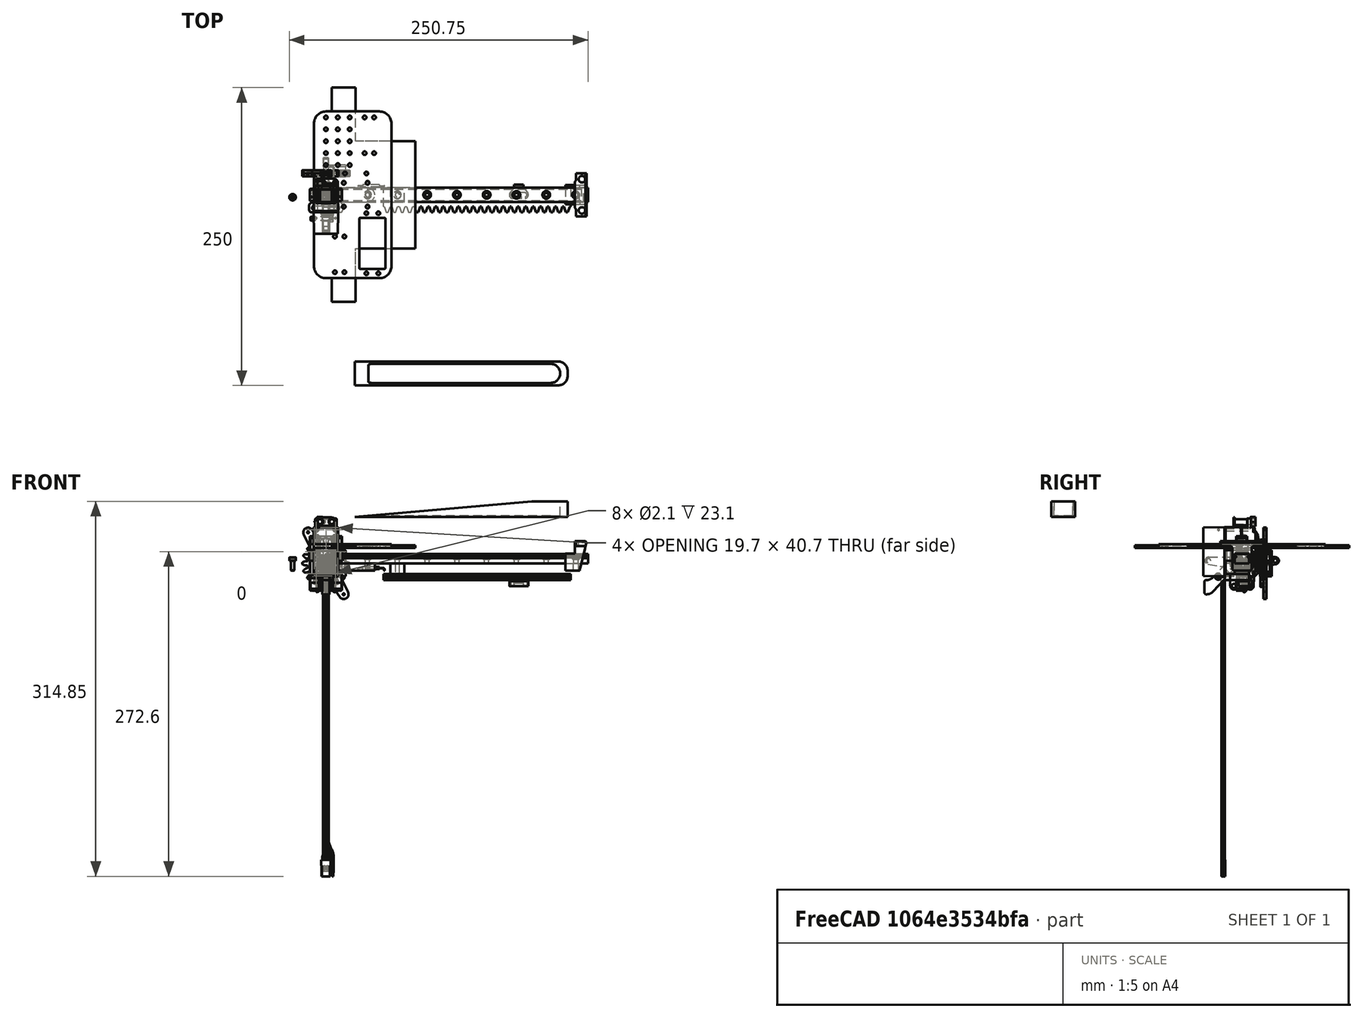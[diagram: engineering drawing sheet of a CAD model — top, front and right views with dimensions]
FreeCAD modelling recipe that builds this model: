
FCSTD DOCUMENT  (FreeCAD 1.0R39285 (Git))
Label: elevateur_canettes
License: All rights reserved
LicenseURL: https://en.wikipedia.org/wiki/All_rights_reserved
objects: Sketcher::SketchObject×58, Part::Feature×46, PartDesign::Pad×32, PartDesign::Pocket×29, PartDesign::Body×22, App::Part×11, Part::FeaturePython×11, PartDesign::Mirrored×11, App::Link×7, PartDesign::LinearPattern×5, PartDesign::Chamfer×4, App::LinkElement×4, PartDesign::PolarPattern×3, PartDesign::FeatureBase×3, PartDesign::MultiTransform×3, PartDesign::Fillet×3, Spreadsheet::Sheet×2, Part::Plane×2, Part::Part2DObjectPython×2, Mesh::Feature×2, +2 more types
note: 456 computed .brp shape members not serialized (recipe doc carries the construction recipe); baked Part::Feature solids carry a one-line shape summary decoded from their .brp
EXTERNAL_REF file=CanaPince.FCStd obj=Part004

FEATURE [Part::Feature] Part__Feature008002002006398  label="MGN12H_EndCap"
  Placement = pos=(5.7441e-12,8.41e-14,21.2) rot=(0,1,0;3.14159rad)
  shape: bbox 26.8 x 9.4 x 5 mm, 23 faces (baked)
FEATURE [Part::Feature] Part__Feature008002002006399  label="MGN12H_EndCap001"
  Placement = pos=(-7.5658e-12,-8.59e-14,-16.2) rot=(0,1,0;3.14159rad)
  shape: bbox 26.8 x 9.4 x 5 mm, 23 faces (baked)
FEATURE [Part::Feature] Part__Feature008002002006400  label="MGN12H_Seal"
  Placement = pos=(-5.6e-15,-0.3,22.7) rot=(0,0,1;0rad)
  shape: bbox 26.8 x 9.4 x 1.7 mm, 155 faces (baked)
FEATURE [Part::Feature] Part__Feature008002002006401  label="MGN12H_Seal001"
  Placement = pos=(-7.2971e-12,-0.3,-22.7) rot=(0,1,0;3.14159rad)
  shape: bbox 26.8 x 9.4 x 1.7 mm, 155 faces (baked)
FEATURE [Part::Feature] Part__Feature008002002006402  label="MGN12H_Cage"
  Placement = pos=(-7.7,-2.54,-20.95) rot=(-0.57735,-0.57735,-0.57735;2.0944rad)
  shape: bbox 3.312 x 0.5 x 42.52 mm, 12 faces (baked)
FEATURE [Part::Feature] Part__Feature008002002006403  label="MGN12H_Cage001"
  Placement = pos=(7.7,-2.79,20.95) rot=(-0.576199,0.576199,0.579647;2.09095rad)
  shape: bbox 3.312 x 0.7505 x 42.52 mm, 12 faces (baked)
FEATURE [Part::Feature] Part__Feature008002002006404  label="MGN12H_Ball"
  Placement = pos=(-6.48,-2.54,19.51) rot=(-0.365574,-0.473745,0.8012;0.619125rad)
  shape: bbox 2.38 x 2.38 x 2.38 mm, 2 faces (baked)
FEATURE [Part::Feature] Part__Feature008002002006405  label="MGN12H_Ball001"
  Placement = pos=(-6.48,-2.54,17.13) rot=(0.592122,0.368399,0.71671;0.865325rad)
  shape: bbox 2.38 x 2.38 x 2.38 mm, 2 faces (baked)
FEATURE [Part::Feature] Part__Feature008002002006406  label="MGN12H_Ball002"
  Placement = pos=(-6.48,-2.54,14.75) rot=(-0.365574,-0.473745,0.8012;0.619125rad)
  shape: bbox 2.38 x 2.38 x 2.38 mm, 2 faces (baked)
FEATURE [Part::Feature] Part__Feature008002002006407  label="MGN12H_Ball003"
  Placement = pos=(-6.48,-2.54,12.37) rot=(-0.365574,-0.473745,0.8012;0.619125rad)
  shape: bbox 2.38 x 2.38 x 2.38 mm, 2 faces (baked)
FEATURE [Part::Feature] Part__Feature008002002006408  label="MGN12H_Ball004"
  Placement = pos=(-6.48,-2.54,9.99) rot=(-0.365574,-0.473745,0.8012;0.619125rad)
  shape: bbox 2.38 x 2.38 x 2.38 mm, 2 faces (baked)
FEATURE [Part::Feature] Part__Feature008002002006409  label="MGN12H_Ball005"
  Placement = pos=(-6.48,-2.54,7.61) rot=(-0.365574,-0.473745,0.8012;0.619125rad)
  shape: bbox 2.38 x 2.38 x 2.38 mm, 2 faces (baked)
FEATURE [Part::Feature] Part__Feature008002002006410  label="MGN12H_Ball006"
  Placement = pos=(-6.48,-2.54,5.23) rot=(-0.365574,-0.473745,0.8012;0.619125rad)
  shape: bbox 2.38 x 2.38 x 2.38 mm, 2 faces (baked)
FEATURE [Part::Feature] Part__Feature008002002006411  label="MGN12H_Ball007"
  Placement = pos=(-6.48,-2.54,2.85) rot=(-0.365574,-0.473745,0.8012;0.619125rad)
  shape: bbox 2.38 x 2.38 x 2.38 mm, 2 faces (baked)
FEATURE [Part::Feature] Part__Feature008002002006412  label="MGN12H_Ball008"
  Placement = pos=(-6.48,-2.54,0.47) rot=(-0.365574,-0.473745,0.8012;0.619125rad)
  shape: bbox 2.38 x 2.38 x 2.38 mm, 2 faces (baked)
FEATURE [Part::Feature] Part__Feature008002002006413  label="MGN12H_Ball009"
  Placement = pos=(-6.48,-2.54,-1.91) rot=(-0.365574,-0.473745,0.8012;0.619125rad)
  shape: bbox 2.38 x 2.38 x 2.38 mm, 2 faces (baked)
FEATURE [Part::Feature] Part__Feature008002002006414  label="MGN12H_Ball010"
  Placement = pos=(-6.48,-2.54,-4.29) rot=(-0.365574,-0.473745,0.8012;0.619125rad)
  shape: bbox 2.38 x 2.38 x 2.38 mm, 2 faces (baked)
FEATURE [Part::Feature] Part__Feature008002002006415  label="MGN12H_Ball011"
  Placement = pos=(-6.48,-2.54,-6.67) rot=(-0.365574,-0.473745,0.8012;0.619125rad)
  shape: bbox 2.38 x 2.38 x 2.38 mm, 2 faces (baked)
FEATURE [Part::Feature] Part__Feature008002002006416  label="MGN12H_Ball012"
  Placement = pos=(-6.48,-2.54,-9.05) rot=(-0.365574,-0.473745,0.8012;0.619125rad)
  shape: bbox 2.38 x 2.38 x 2.38 mm, 2 faces (baked)
FEATURE [Part::Feature] Part__Feature008002002006417  label="MGN12H_Ball013"
  Placement = pos=(-6.48,-2.54,-11.43) rot=(-0.365574,-0.473745,0.8012;0.619125rad)
  shape: bbox 2.38 x 2.38 x 2.38 mm, 2 faces (baked)
FEATURE [Part::Feature] Part__Feature008002002006418  label="MGN12H_Ball014"
  Placement = pos=(-6.48,-2.54,-13.81) rot=(-0.365574,-0.473745,0.8012;0.619125rad)
  shape: bbox 2.38 x 2.38 x 2.38 mm, 2 faces (baked)
FEATURE [Part::Feature] Part__Feature008002002006419  label="MGN12H_Ball015"
  Placement = pos=(-6.48,-2.54,-16.19) rot=(-0.365574,-0.473745,0.8012;0.619125rad)
  shape: bbox 2.38 x 2.38 x 2.38 mm, 2 faces (baked)
FEATURE [Part::Feature] Part__Feature008002002006420  label="MGN12H_Ball016"
  Placement = pos=(-6.48,-2.54,-19.51) rot=(0.61831,0.691205,-0.374071;3.60491rad)
  shape: bbox 2.38 x 2.38 x 2.38 mm, 2 faces (baked)
FEATURE [Part::Feature] Part__Feature008002002006421  label="MGN12H_Ball017"
  Placement = pos=(6.48,-2.54,19.5319) rot=(0.61831,0.691205,-0.374071;3.60491rad)
  shape: bbox 2.38 x 2.38 x 2.38 mm, 2 faces (baked)
FEATURE [Part::Feature] Part__Feature008002002006422  label="MGN12H_Ball018"
  Placement = pos=(6.48,-2.54,17.1519) rot=(0.61831,0.691205,-0.374071;3.60491rad)
  shape: bbox 2.38 x 2.38 x 2.38 mm, 2 faces (baked)
FEATURE [Part::Feature] Part__Feature008002002006423  label="MGN12H_Ball019"
  Placement = pos=(6.48,-2.54,14.7719) rot=(0.61831,0.691205,-0.374071;3.60491rad)
  shape: bbox 2.38 x 2.38 x 2.38 mm, 2 faces (baked)
FEATURE [Part::Feature] Part__Feature008002002006424  label="MGN12H_Ball020"
  Placement = pos=(6.48,-2.54,12.3919) rot=(0.61831,0.691205,-0.374071;3.60491rad)
  shape: bbox 2.38 x 2.38 x 2.38 mm, 2 faces (baked)
FEATURE [Part::Feature] Part__Feature008002002006425  label="MGN12H_Ball021"
  Placement = pos=(6.48,-2.54,10.0119) rot=(0.61831,0.691205,-0.374071;3.60491rad)
  shape: bbox 2.38 x 2.38 x 2.38 mm, 2 faces (baked)
FEATURE [Part::Feature] Part__Feature008002002006426  label="MGN12H_Ball022"
  Placement = pos=(6.48,-2.54,7.63187) rot=(0.61831,0.691205,-0.374071;3.60491rad)
  shape: bbox 2.38 x 2.38 x 2.38 mm, 2 faces (baked)
FEATURE [Part::Feature] Part__Feature008002002006427  label="MGN12H_Ball023"
  Placement = pos=(6.48,-2.54,5.25187) rot=(0.61831,0.691205,-0.374071;3.60491rad)
  shape: bbox 2.38 x 2.38 x 2.38 mm, 2 faces (baked)
FEATURE [Part::Feature] Part__Feature008002002006428  label="MGN12H_Ball024"
  Placement = pos=(6.48,-2.54,2.87187) rot=(0.61831,0.691205,-0.374071;3.60491rad)
  shape: bbox 2.38 x 2.38 x 2.38 mm, 2 faces (baked)
FEATURE [Part::Feature] Part__Feature008002002006429  label="MGN12H_Ball025"
  Placement = pos=(6.48,-2.54,0.491867) rot=(0.61831,0.691205,-0.374071;3.60491rad)
  shape: bbox 2.38 x 2.38 x 2.38 mm, 2 faces (baked)
FEATURE [Part::Feature] Part__Feature008002002006430  label="MGN12H_Ball026"
  Placement = pos=(6.48,-2.54,-1.88813) rot=(0.61831,0.691205,-0.374071;3.60491rad)
  shape: bbox 2.38 x 2.38 x 2.38 mm, 2 faces (baked)
FEATURE [Part::Feature] Part__Feature008002002006431  label="MGN12H_Ball027"
  Placement = pos=(6.48,-2.54,-4.26813) rot=(0.61831,0.691205,-0.374071;3.60491rad)
  shape: bbox 2.38 x 2.38 x 2.38 mm, 2 faces (baked)
FEATURE [Part::Feature] Part__Feature008002002006432  label="MGN12H_Ball028"
  Placement = pos=(6.48,-2.54,-6.64813) rot=(0.61831,0.691205,-0.374071;3.60491rad)
  shape: bbox 2.38 x 2.38 x 2.38 mm, 2 faces (baked)
FEATURE [Part::Feature] Part__Feature008002002006433  label="MGN12H_Ball029"
  Placement = pos=(6.48,-2.54,-9.02813) rot=(0.61831,0.691205,-0.374071;3.60491rad)
  shape: bbox 2.38 x 2.38 x 2.38 mm, 2 faces (baked)
FEATURE [Part::Feature] Part__Feature008002002006434  label="MGN12H_Ball030"
  Placement = pos=(6.48,-2.54,-11.4081) rot=(0.61831,0.691205,-0.374071;3.60491rad)
  shape: bbox 2.38 x 2.38 x 2.38 mm, 2 faces (baked)
FEATURE [Part::Feature] Part__Feature008002002006435  label="MGN12H_Ball031"
  Placement = pos=(6.48,-2.54,-13.7881) rot=(0.61831,0.691205,-0.374071;3.60491rad)
  shape: bbox 2.38 x 2.38 x 2.38 mm, 2 faces (baked)
FEATURE [Part::Feature] Part__Feature008002002006436  label="MGN12H_Ball032"
  Placement = pos=(6.48,-2.54,-16.1681) rot=(0.61831,0.691205,-0.374071;3.60491rad)
  shape: bbox 2.38 x 2.38 x 2.38 mm, 2 faces (baked)
FEATURE [Part::Feature] Part__Feature008002002006437  label="MGN12H_Ball033"
  Placement = pos=(6.48,-2.54,-19.5093) rot=(0.656664,0.517892,-0.548252;3.76753rad)
  shape: bbox 2.38 x 2.38 x 2.38 mm, 2 faces (baked)
FEATURE [Part::Feature] Part__Feature226  label="MGN12H_Body"
  shape: bbox 27 x 10.2 x 48.24 mm, 183 faces (baked)
FEATURE [App::Part] MGN12H001
  Group = -> [Part__Feature226,Part__Feature008002002006398,Part__Feature008002002006399,Part__Feature008002002006400,Part__Feature008002002006401,Part__Feature008002002006402,Part__Feature008002002006403,Part__Feature008002002006404,Part__Feature008002002006405,Part__Feature008002002006406,Part__Feature008002002006407,Part__Feature008002002006408,Part__Feature008002002006409,Part__Feature008002002006410,+27 more]
  Origin = -> Origin263
  Placement = pos=(25,0,8.05) rot=(0.57735,0.57735,0.57735;2.0944rad)
FEATURE [Sketcher::SketchObject] Sketch186
  ArcFitTolerance = 0
  AttachmentSupport = -> [YZ_Plane261]
  FullyConstrained = true
  MakeInternals = false
  MapMode = 5
  Placement = pos=(0,0,0) rot=(0.57735,0.57735,0.57735;2.0944rad)
  sketch-geometry (4):
    g0: LineSegment StartX=-6 StartY=0 StartZ=0 EndX=6 EndY=0 EndZ=0
    g1: LineSegment StartX=6 StartY=0 StartZ=0 EndX=6 EndY=8 EndZ=0
    g2: LineSegment StartX=6 StartY=8 StartZ=0 EndX=-6 EndY=8 EndZ=0
    g3: LineSegment StartX=-6 StartY=8 StartZ=0 EndX=-6 EndY=0 EndZ=0
  constraints (11):
    c: Coincident(g0,g1)
    c: Coincident(g1,g2)
    c: Coincident(g2,g3)
    c: Coincident(g3,g0)
    c: Horizontal(g0)
    c: Horizontal(g2)
    c: Vertical(g1)
    c: Vertical(g3)
    c: Symmetric(g0,g0,g-1)
    c: DistanceX(g0,g0) = 12  'width'
    c: DistanceY(g1,g1) = 8  'height'
FEATURE [PartDesign::Pad] Pad093
  Direction = (1,0,0)
  Length = 220
  Length2 = 10
  Placement = pos=(0,0,0) rot=(0.57735,0.57735,0.57735;2.0944rad)
  Profile = -> Sketch186
  ReferenceAxis = -> Sketch186 [N_Axis]
  Suppressed = false
  Type = 0
  expr: Length = Spreadsheet002.length
FEATURE [Sketcher::SketchObject] Sketch187
  ArcFitTolerance = 0
  AttachmentSupport = -> [YZ_Plane261]
  FullyConstrained = true
  MakeInternals = false
  MapMode = 5
  Placement = pos=(0,0,0) rot=(0.57735,-0.57735,-0.57735;2.0944rad)
  expr: Constraints[13] = <<Sketch186>>.Constraints.width / 2 + 0.3 mm
  sketch-geometry (10):
    g0: ArcOfCircle CenterX=-6.3 CenterY=5.5 CenterZ=0 NormalX=0 NormalY=0 NormalZ=1 AngleXU=0 Radius=1.2 StartAngle=0.429775 EndAngle=5.85341
    g1: LineSegment StartX=-5.20913 StartY=6 StartZ=0 EndX=-4.70913 EndY=6 EndZ=0
    g2: LineSegment StartX=-4.70913 StartY=6 StartZ=0 EndX=-4.70913 EndY=5 EndZ=0
    g3: LineSegment StartX=-4.70913 StartY=5 StartZ=0 EndX=-5.20913 EndY=5 EndZ=0
    g4: LineSegment [constr] StartX=-6.3 StartY=5.5 StartZ=0 EndX=-4.70913 EndY=5.5 EndZ=0
    g5: ArcOfCircle CenterX=6.3 CenterY=5.5 CenterZ=0 NormalX=0 NormalY=0 NormalZ=1 AngleXU=0 Radius=1.2 StartAngle=3.57137 EndAngle=8.995
    g6: LineSegment StartX=5.20913 StartY=6 StartZ=0 EndX=4.70913 EndY=6 EndZ=0
    g7: LineSegment StartX=4.70913 StartY=6 StartZ=0 EndX=4.70913 EndY=5 EndZ=0
    g8: LineSegment StartX=4.70913 StartY=5 StartZ=0 EndX=5.20913 EndY=5 EndZ=0
    g9: LineSegment [constr] StartX=6.3 StartY=5.5 StartZ=0 EndX=4.70913 EndY=5.5 EndZ=0
  constraints (29):
    c: Horizontal(g1)
    c: Coincident(g2,g1)
    c: Vertical(g2)
    c: Coincident(g3,g2)
    c: Horizontal(g3)
    c: Coincident(g4,g0)
    c: Horizontal(g4)
    c: Symmetric(g2,g1,g4)
    c: Coincident(g0,g3)
    c: Coincident(g0,g1)
    c: DistanceY(g2,g2) = 1
    c: DistanceX(g1,g1) = 0.5
    c: DistanceY(g-1,g0) = 5.5
    c: DistanceX(g0,g-1) = 6.3
    c: Horizontal(g6)
    c: Coincident(g7,g6)
    c: Vertical(g7)
    c: Coincident(g8,g7)
    c: Horizontal(g8)
    c: Coincident(g9,g5)
    c: Horizontal(g9)
    c: Symmetric(g7,g6,g9)
    c: Coincident(g5,g8)
    c: Coincident(g5,g6)
    c: Diameter(g5) = 2.4
    c: Symmetric(g4,g9,g-2)
    c: Equal(g2,g7)
    c: Equal(g1,g6)
    c: Equal(g0,g5)
FEATURE [PartDesign::Pocket] Pocket008  label="Balls cut001"
  BaseFeature = -> Pad093
  Direction = (1,0,0)
  Length = 5
  Length2 = 5
  Placement = pos=(0,0,0) rot=(0.57735,0.57735,0.57735;2.0944rad)
  Profile = -> Sketch187
  ReferenceAxis = -> Sketch187 [N_Axis]
  Suppressed = false
  Type = 1
FEATURE [Sketcher::SketchObject] Sketch188
  ArcFitTolerance = 0
  AttachmentOffset = pos=(10,0,0) rot=(0,0,1;1.5708rad)
  AttachmentSupport = -> [XY_Plane261]
  FullyConstrained = true
  MakeInternals = false
  MapMode = 5
  Placement = pos=(10,0,0) rot=(0,0,1;1.5708rad)
  expr: .AttachmentOffset.Base.x = Spreadsheet002.offset
  sketch-geometry (1):
    g0: Circle CenterX=0 CenterY=0 CenterZ=0 NormalX=0 NormalY=0 NormalZ=1 AngleXU=0 Radius=1.75
  constraints (2):
    c: Coincident(g0,g-1)
    c: Diameter(g0) = 3.5
FEATURE [PartDesign::Pocket] Pocket009  label="Screw hole001"
  BaseFeature = -> Pocket008
  Direction = (0,0,-1)
  Length = 5
  Length2 = 5
  Midplane = true
  Placement = pos=(0,0,0) rot=(0.57735,0.57735,0.57735;2.0944rad)
  Profile = -> Sketch188
  ReferenceAxis = -> Sketch188 [N_Axis]
  Suppressed = false
  Type = 1
FEATURE [Sketcher::SketchObject] Sketch189
  ArcFitTolerance = 0
  AttachmentOffset = pos=(10,0,8) rot=(0,0,1;1.5708rad)
  AttachmentSupport = -> [XY_Plane261]
  FullyConstrained = true
  MakeInternals = false
  MapMode = 5
  Placement = pos=(10,0,8) rot=(0,0,1;1.5708rad)
  expr: .AttachmentOffset.Base.x = Spreadsheet002.offset
  expr: .AttachmentOffset.Base.z = Sketch186.Constraints.height
  sketch-geometry (1):
    g0: Circle CenterX=0 CenterY=0 CenterZ=0 NormalX=0 NormalY=0 NormalZ=1 AngleXU=0 Radius=3
  constraints (2):
    c: Coincident(g0,g-1)
    c: Diameter(g0) = 6
FEATURE [PartDesign::Pocket] Pocket072  label="Screw head cut001"
  BaseFeature = -> Pocket009
  Direction = (0,0,-1)
  Length = 4.5
  Length2 = 5
  Placement = pos=(0,0,0) rot=(0.57735,0.57735,0.57735;2.0944rad)
  Profile = -> Sketch189
  ReferenceAxis = -> Sketch189 [N_Axis]
  Suppressed = false
  Type = 0
FEATURE [PartDesign::Chamfer] Chamfer005
  Angle = 45
  Base = -> Pocket072 [Edge47]
  BaseFeature = -> Pocket072
  ChamferType = 0
  FlipDirection = false
  Placement = pos=(0,0,0) rot=(0.57735,0.57735,0.57735;2.0944rad)
  Size = 0.2
  Size2 = 1
  SupportTransform = false
  Suppressed = false
  UseAllEdges = false
FEATURE [PartDesign::LinearPattern] LinearPattern002
  BaseFeature = -> Chamfer005
  Direction = -> Sketch188 [V_Axis]
  Length = 200
  Mode = 0
  Occurrences = 9
  Offset = 25
  Originals = -> [Pocket009,Pocket072,Chamfer005]
  Placement = pos=(0,0,0) rot=(0.57735,0.57735,0.57735;2.0944rad)
  Reversed = true
  Suppressed = false
  TransformMode = 0
  expr: Length = Spreadsheet002.distance
  expr: Occurrences = Spreadsheet002.holes_number
FEATURE [PartDesign::Body] Body071  label="Hiwin rail MGN12R"
  AllowCompound = false
  Group = -> [Sketch186,Pad093,Sketch187,Pocket008,Sketch188,Pocket009,Sketch189,Pocket072,Chamfer005,LinearPattern002]
  Origin = -> Origin264
  Tip = -> LinearPattern002
FEATURE [Sketcher::SketchObject] Sketch190
  ArcFitTolerance = 1e-06
  AttachmentSupport = -> [XZ_Plane265]
  FullyConstrained = true
  MakeInternals = false
  MapMode = 5
  Placement = pos=(0,0,0) rot=(0,0.707107,0.707107;3.14159rad)
  sketch-geometry (9):
    g0: LineSegment StartX=-45 StartY=50 StartZ=0 EndX=-45 EndY=0 EndZ=0
    g1: LineSegment StartX=45 StartY=0 StartZ=0 EndX=45 EndY=50 EndZ=0
    g2: LineSegment StartX=45 StartY=50 StartZ=0 EndX=-45 EndY=50 EndZ=0
    g3: LineSegment StartX=-90 StartY=0 StartZ=0 EndX=-90 EndY=-20 EndZ=0
    g4: LineSegment StartX=-90 StartY=-20 StartZ=0 EndX=90 EndY=-20 EndZ=0
    g5: LineSegment StartX=90 StartY=-20 StartZ=0 EndX=90 EndY=0 EndZ=0
    g6: LineSegment StartX=90 StartY=0 StartZ=0 EndX=45 EndY=0 EndZ=0
    g7: LineSegment StartX=-45 StartY=0 StartZ=0 EndX=-90 EndY=0 EndZ=0
    g8: Circle CenterX=-10 CenterY=10 CenterZ=0 NormalX=0 NormalY=0 NormalZ=1 AngleXU=0 Radius=2
  constraints (25):
    c: Coincident(g1,g2)
    c: Coincident(g2,g0)
    c: Vertical(g0)
    c: Vertical(g1)
    c: PointOnObject(g1,g-1)
    c: Coincident(g3,g4)
    c: Coincident(g4,g5)
    c: Coincident(g5,g6)
    c: Coincident(g7,g3)
    c: Vertical(g3)
    c: Vertical(g5)
    c: Horizontal(g4)
    c: Horizontal(g6)
    c: Coincident(g0,g7)
    c: Coincident(g1,g6)
    c: Horizontal(g7)
    c: Symmetric(g1,g0,g-2)
    c: Symmetric(g3,g5,g-2)
    c: Diameter(g8) = 4
    c: DistanceX(g8,g-1) = 10
    c: Distance(g8,g-1) = 10
    c: DistanceX(g2,g2) = 90
    c: DistanceX(g4,g4) = 180
    c: DistanceY(g0,g0) = 50
    c: DistanceY(g5,g5) = 20
FEATURE [PartDesign::Pad] Pad094
  Direction = (0,1,-2e-16)
  Length = 2
  Length2 = 10
  Placement = pos=(0,0,0) rot=(1,0,0;1.5708rad)
  Profile = -> Sketch190 [Edge4,Edge3,Edge2,Edge1,Edge8,Edge7,Edge6,Edge5]
  ReferenceAxis = -> Sketch190 [N_Axis]
  Suppressed = false
  Type = 0
FEATURE [PartDesign::Pocket] Pocket073
  BaseFeature = -> Pad094
  Direction = (0,-1,2e-16)
  Length = 5
  Length2 = 5
  Placement = pos=(0,0,0) rot=(1,0,0;1.5708rad)
  Profile = -> Sketch190 [Edge9]
  ReferenceAxis = -> Sketch190 [N_Axis]
  Reversed = true
  Suppressed = false
  Type = 0
FEATURE [PartDesign::PolarPattern] PolarPattern010
  Angle = 360
  Axis = -> Sketch190 [N_Axis]
  BaseFeature = -> Pocket073
  Mode = 0
  Occurrences = 4
  Offset = 120
  Originals = -> [Pocket073]
  Placement = pos=(0,0,0) rot=(1,0,0;1.5708rad)
  Suppressed = false
  TransformMode = 0
FEATURE [Sketcher::SketchObject] Sketch191
  ArcFitTolerance = 1e-06
  AttachmentSupport = -> [PolarPattern010]
  FullyConstrained = true
  MakeInternals = false
  MapMode = 5
  Placement = pos=(0,2,0) rot=(-1,0,0;1.5708rad)
FEATURE [PartDesign::Body] Body072  label="plaque_support_leve_gradin"
  AllowCompound = false
  Group = -> [Sketch190,Pad094,Pocket073,PolarPattern010,Sketch191]
  Origin = -> Origin268
  Placement = pos=(25,-2.9e-15,13) rot=(0.57735,0.57735,0.57735;2.0944rad)
  Tip = -> PolarPattern010
FEATURE [Spreadsheet::Sheet] Spreadsheet002  label="Spreadsheet_MGN12"
  cells = A1='Length rail; B1='Длина рельсы, мм; C1(length)=220; D1=325; A2='Holes distance; B2='Расстояние между отверстиями; C2(holes_distance)=25; A3='Holes number; B3='Количество отверстий; C3(holes_number)==floor((length - min_offset * 2) / holes_distance) + 1; A4='Distance end holes; B4='Расстояние между центрами крайних отверстий; C4(distance)==holes_distance * (holes_number - 1); A5='Offset 1st hole; B5='Позиция 1го отверстия; C5(offset)==(length - distance) / 2; A6='Min offset 1st hole; B6='Минимальное расстояние от края до центра 1го отверстия; C6(min_offset)=5
FEATURE [App::Part] Part002003  label="Hiwin MGN013"
  Group = -> [Body071,Spreadsheet002]
  Origin = -> Origin265
FEATURE [Part::Feature] Part__Feature001  label="DA 20_servo001"
  shape: bbox 20.7 x 51.21 x 300.6 mm, 536 faces (baked)
FEATURE [Part::Feature] Part__Feature002  label="1641.21"
  Placement = pos=(-1.33e-14,20.6,2.41e-14) rot=(0,1,0;2.61799rad)
  shape: bbox 24.98 x 5 x 35.96 mm, 19 faces (baked)
FEATURE [Part::Feature] Part__Feature003  label="1641.20"
  Placement = pos=(0,20.6,-1e-16) rot=(0,-1,0;0.523599rad)
  shape: bbox 38 x 5 x 59.96 mm, 25 faces (baked)
FEATURE [Part::Feature] Part__Feature004  label="socket head thin cap screw_din_DIN 7984 - M3 x 6 --- 6N"
  Placement = pos=(8e-16,21.2,-7e-16) rot=(0.694747,-0.694747,0.186157;3.50969rad)
  shape: bbox 5.75 x 8 x 5.75 mm, 21 faces (baked)
FEATURE [Part::Feature] Part__Feature005  label="DA 20_servo002"
  shape: bbox 20.7 x 51.21 x 300.6 mm, 536 faces (baked)
FEATURE [Part::Plane] Plane  label="Plan"
  AttacherType = Attacher::AttachEngine3D
  Length = 100
  Placement = pos=(-50,14.15,-50) rot=(1,0,0;1.5708rad)
  Width = 100
FEATURE [Part::Plane] Plane003  label="Plan003"
  AttacherType = Attacher::AttachEngine3D
  Length = 100
  Placement = pos=(-50,-105,-16.5) rot=(1,0,0;0rad)
  Width = 100
FEATURE [Part::FeaturePython] Slice  # WARN: FeaturePython — macro-defined, semantics opaque (R4)
  Base = -> Part__Feature001
  Mode = 1
  Tolerance = 0
  Tools = -> [Plane]
FEATURE [Part::FeaturePython] Slice_child0  label="Slice.0"  # WARN: FeaturePython — macro-defined, semantics opaque (R4)
  Base = -> Slice
  FilterType = 1
  Invert = false
  OverrideMaxVal = 0
  WindowFrom = 80
  WindowTo = 100
  items = 0
FEATURE [Part::FeaturePython] Slice001  # WARN: FeaturePython — macro-defined, semantics opaque (R4)
  Base = -> Slice_child0
  Mode = 1
  Tolerance = 0
  Tools = -> [Plane003]
FEATURE [Part::FeaturePython] Slice_child1  label="Slice.1"  # WARN: FeaturePython — macro-defined, semantics opaque (R4)
  Base = -> Slice
  FilterType = 1
  Invert = false
  OverrideMaxVal = 0
  WindowFrom = 80
  WindowTo = 100
  items = 1
FEATURE [Part::FeaturePython] Slice001_child1  label="Slice001.1"  # WARN: FeaturePython — macro-defined, semantics opaque (R4)
  Base = -> Slice001
  FilterType = 1
  Invert = false
  OverrideMaxVal = 0
  WindowFrom = 80
  WindowTo = 100
  items = 1
FEATURE [Part::FeaturePython] Slice001_child0  label="Slice001.0"  # WARN: FeaturePython — macro-defined, semantics opaque (R4)
  Base = -> Slice001
  FilterType = 1
  Invert = false
  OverrideMaxVal = 0
  WindowFrom = 80
  WindowTo = 100
  items = 0
FEATURE [PartDesign::FeatureBase] BaseFeature
  BaseFeature = -> Slice_child1
  Suppressed = false
FEATURE [PartDesign::Body] Body  label="pignon"
  AllowCompound = false
  BaseFeature = -> Slice_child1
  Group = -> [BaseFeature]
  Origin = -> Origin001
  Tip = -> BaseFeature
FEATURE [PartDesign::FeatureBase] BaseFeature001
  BaseFeature = -> Slice001_child0
  Suppressed = false
FEATURE [PartDesign::Body] Body001  label="corps"
  AllowCompound = false
  BaseFeature = -> Slice001_child0
  Group = -> [BaseFeature001]
  Origin = -> Origin002
  Tip = -> BaseFeature001
FEATURE [Sketcher::SketchObject] Sketch
  ArcFitTolerance = 1e-06
  AttachmentSupport = -> [XZ_Plane003]
  FullyConstrained = true
  MakeInternals = false
  MapMode = 5
  Placement = pos=(0,0,0) rot=(1,0,0;1.5708rad)
  sketch-geometry (4):
    g0: Circle CenterX=0 CenterY=0 CenterZ=0 NormalX=0 NormalY=0 NormalZ=1 AngleXU=0 Radius=1.5
    g1: Circle CenterX=0 CenterY=0 CenterZ=0 NormalX=0 NormalY=0 NormalZ=1 AngleXU=0 Radius=2.75
    g2: Circle CenterX=0 CenterY=0 CenterZ=0 NormalX=0 NormalY=0 NormalZ=1 AngleXU=0 Radius=4.75
    g3: Circle CenterX=0 CenterY=0 CenterZ=0 NormalX=0 NormalY=0 NormalZ=1 AngleXU=0 Radius=10
  constraints (8):
    c: Diameter(g0) = 3
    c: Coincident(g0,g-1)
    c: Diameter(g1) = 5.5
    c: Coincident(g1,g0)
    c: Diameter(g2) = 9.5
    c: Coincident(g2,g0)
    c: Diameter(g3) = 20
    c: Coincident(g3,g0)
FEATURE [PartDesign::Pad] Pad
  Direction = (0,-1,2e-16)
  Length = 5
  Length2 = 10
  Placement = pos=(0,0,0) rot=(1,0,0;1.5708rad)
  Profile = -> Sketch [Edge3,Edge2]
  ReferenceAxis = -> Sketch [N_Axis]
  Suppressed = false
  Type = 0
FEATURE [PartDesign::Pad] Pad001
  BaseFeature = -> Pad
  Direction = (0,-1,2e-16)
  Length = 2
  Length2 = 10
  Placement = pos=(0,0,0) rot=(1,0,0;1.5708rad)
  Profile = -> Sketch [Edge1,Edge3]
  ReferenceAxis = -> Sketch [N_Axis]
  Suppressed = false
  Type = 0
FEATURE [PartDesign::Pocket] Pocket
  BaseFeature = -> Pad001
  Direction = (0,1,-2e-16)
  Length = 0.6
  Length2 = 5
  Placement = pos=(0,0,0) rot=(1,0,0;1.5708rad)
  Profile = -> Sketch [Edge1,Edge2]
  ReferenceAxis = -> Sketch [N_Axis]
  Reversed = true
  Suppressed = false
  Type = 0
FEATURE [PartDesign::Pad] Pad002
  BaseFeature = -> Pocket
  Direction = (0,-1,2e-16)
  Length = 2
  Length2 = 10
  Placement = pos=(0,0,0) rot=(1,0,0;1.5708rad)
  Profile = -> Sketch [Edge2,Edge4]
  ReferenceAxis = -> Sketch [N_Axis]
  Suppressed = false
  Type = 0
FEATURE [Sketcher::SketchObject] Sketch001
  ArcFitTolerance = 1e-06
  AttachmentSupport = -> [Pad002]
  FullyConstrained = true
  MakeInternals = false
  MapMode = 5
  Placement = pos=(0,0,0) rot=(-1,0,0;1.5708rad)
  sketch-geometry (1):
    g0: Circle CenterX=0 CenterY=7 CenterZ=0 NormalX=0 NormalY=0 NormalZ=1 AngleXU=0 Radius=1
  constraints (3):
    c: Diameter(g0) = 2
    c: PointOnObject(g0,g-2)
    c: DistanceY(g-1,g0) = 7
FEATURE [PartDesign::Pocket] Pocket001
  BaseFeature = -> Pad002
  Direction = (0,-1,-2e-16)
  Length = 5
  Length2 = 5
  Placement = pos=(0,0,0) rot=(1,0,0;1.5708rad)
  Profile = -> Sketch001
  ReferenceAxis = -> Sketch001 [N_Axis]
  Suppressed = false
  Type = 0
FEATURE [PartDesign::PolarPattern] PolarPattern
  Angle = 360
  Axis = -> Sketch001 [N_Axis]
  BaseFeature = -> Pocket001
  Mode = 0
  Occurrences = 12
  Offset = 120
  Originals = -> [Pocket001]
  Placement = pos=(0,0,0) rot=(1,0,0;1.5708rad)
  Suppressed = false
  TransformMode = 0
FEATURE [PartDesign::Body] Body002  label="attachement_base"
  AllowCompound = false
  Group = -> [Sketch,Pad,Pad001,Pocket,Pad002,Sketch001,Pocket001,PolarPattern]
  Origin = -> Origin003
  Placement = pos=(0,20.6,0) rot=(0,0,1;0rad)
  Tip = -> PolarPattern
FEATURE [Sketcher::SketchObject] Sketch002
  ArcFitTolerance = 1e-06
  AttachmentSupport = -> [XZ_Plane004]
  FullyConstrained = true
  MakeInternals = false
  MapMode = 5
  Placement = pos=(0,0,0) rot=(1,0,0;1.5708rad)
  sketch-geometry (4):
    g0: Circle CenterX=0 CenterY=0 CenterZ=0 NormalX=0 NormalY=0 NormalZ=1 AngleXU=0 Radius=1.5
    g1: Circle CenterX=0 CenterY=0 CenterZ=0 NormalX=0 NormalY=0 NormalZ=1 AngleXU=0 Radius=2.75
    g2: Circle CenterX=0 CenterY=0 CenterZ=0 NormalX=0 NormalY=0 NormalZ=1 AngleXU=0 Radius=4.75
    g3: Circle CenterX=0 CenterY=0 CenterZ=0 NormalX=0 NormalY=0 NormalZ=1 AngleXU=0 Radius=20
  constraints (8):
    c: Diameter(g0) = 3
    c: Coincident(g0,g-1)
    c: Diameter(g1) = 5.5
    c: Coincident(g1,g0)
    c: Diameter(g2) = 9.5
    c: Coincident(g2,g0)
    c: Diameter(g3) = 40
    c: Coincident(g3,g0)
FEATURE [PartDesign::Pad] Pad003
  Direction = (0,-1,2e-16)
  Length = 5
  Length2 = 10
  Placement = pos=(0,0,0) rot=(1,0,0;1.5708rad)
  Profile = -> Sketch002 [Edge3,Edge2]
  ReferenceAxis = -> Sketch002 [N_Axis]
  Suppressed = false
  Type = 0
FEATURE [PartDesign::Pad] Pad004
  BaseFeature = -> Pad003
  Direction = (0,-1,2e-16)
  Length = 2
  Length2 = 10
  Placement = pos=(0,0,0) rot=(1,0,0;1.5708rad)
  Profile = -> Sketch002 [Edge1,Edge3]
  ReferenceAxis = -> Sketch002 [N_Axis]
  Suppressed = false
  Type = 0
FEATURE [PartDesign::Pocket] Pocket002
  BaseFeature = -> Pad004
  Direction = (0,1,-2e-16)
  Length = 0.6
  Length2 = 5
  Placement = pos=(0,0,0) rot=(1,0,0;1.5708rad)
  Profile = -> Sketch002 [Edge1,Edge2]
  ReferenceAxis = -> Sketch002 [N_Axis]
  Reversed = true
  Suppressed = false
  Type = 0
FEATURE [PartDesign::Body] Body003  label="pignon001"
  AllowCompound = false
  Group = -> [Sketch002,Pad003,Pad004,Pocket002]
  Origin = -> Origin004
  Placement = pos=(0,20.6,0) rot=(0,1,0;4.71239rad)
  Tip = -> Pocket002
FEATURE [Sketcher::SketchObject] Sketch003
  ArcFitTolerance = 1e-06
  AttachmentSupport = -> [XY_Plane007]
  FullyConstrained = true
  MakeInternals = false
  MapMode = 5
  sketch-geometry (1):
    g0: Circle CenterX=0 CenterY=0 CenterZ=0 NormalX=0 NormalY=0 NormalZ=1 AngleXU=0 Radius=4.75
  constraints (2):
    c: Diameter(g0) = 9.5
    c: Coincident(g0,g-1)
FEATURE [Part::Part2DObjectPython] InvoluteGear  # Draft 2D object (typed FeaturePython)
  AddendumCoefficient = 1
  DedendumCoefficient = 1.25
  ExternalGear = true
  HighPrecision = true
  Modules = 2
  NumberOfTeeth = 18
  PressureAngle = 20
  ProfileShiftCoefficient = 0
  RootFilletCoefficient = 0.38
FEATURE [PartDesign::Pad] Pad005
  Direction = (0,0,1)
  Length = 5
  Length2 = 10
  Profile = -> InvoluteGear
  ReferenceAxis = -> InvoluteGear [N_Axis]
  Reversed = true
  Suppressed = false
  Type = 0
FEATURE [PartDesign::Pocket] Pocket003
  BaseFeature = -> Pad005
  Direction = (0,0,-1)
  Length = 5
  Length2 = 5
  Midplane = true
  Profile = -> Sketch003
  ReferenceAxis = -> Sketch003 [N_Axis]
  Suppressed = false
  Type = 1
FEATURE [PartDesign::Body] Body005  label="pignon002"
  AllowCompound = false
  Group = -> [InvoluteGear,Pad005,Sketch003,Pocket003]
  Origin = -> Origin007
  Placement = pos=(0,20.6,-4.4e-15) rot=(1,0,0;4.71239rad)
  Tip = -> Pocket003
FEATURE [App::Part] Part  label="pignon_servo"
  Group = -> [Body003,Body005]
  Origin = -> Origin006
  Placement = pos=(0,0,0) rot=(0,1,0;4.50295rad)
FEATURE [Part::FeaturePython] InvoluteRack  # WARN: FeaturePython — macro-defined, semantics opaque (R4)
  AttacherType = Attacher::AttachEngine3D
  Placement = pos=(51.5,-12.5,-10.5) rot=(0,0,1;4.71239rad)
  add_endings = true
  clearance = 0.25
  double_helix = false
  head = 0
  head_fillet = 0
  height = 5
  helix_angle = 0
  module = 2
  num_teeth = 25
  pressure_angle = 20
  properties_from_tool = false
  root_fillet = 0
  simplified = false
  thickness = 16
  transverse_pitch = 6.28319
  version = 1.3.0
FEATURE [PartDesign::FeatureBase] BaseFeature002
  BaseFeature = -> InvoluteRack
  Suppressed = false
FEATURE [Sketcher::SketchObject] Sketch192
  ArcFitTolerance = 1e-06
  AttachmentSupport = -> [BaseFeature002]
  FullyConstrained = true
  MakeInternals = false
  MapMode = 5
  Placement = pos=(0,0,5) rot=(0,0,1;0rad)
  sketch-geometry (1):
    g0: Circle CenterX=-12.5 CenterY=8.5 CenterZ=0 NormalX=0 NormalY=0 NormalZ=1 AngleXU=0 Radius=1.7
  constraints (3):
    c: DistanceX(g0) = -12.5
    c: DistanceY(g0) = 8.5
    c: Diameter(g0) = 3.4
FEATURE [PartDesign::Pocket] Pocket074
  BaseFeature = -> BaseFeature002
  Direction = (0,0,-1)
  Length = 5
  Length2 = 5
  Midplane = true
  Profile = -> Sketch192
  ReferenceAxis = -> Sketch192 [N_Axis]
  Suppressed = false
  Type = 1
FEATURE [PartDesign::LinearPattern] LinearPattern
  BaseFeature = -> Pocket074
  Direction = -> Sketch192 [V_Axis]
  Length = 150
  Mode = 0
  Occurrences = 7
  Offset = 25
  Originals = -> [Pocket074]
  Suppressed = false
  TransformMode = 0
FEATURE [Spreadsheet::Sheet] Spreadsheet
  cells = A1='N=Vrot DA20 [tr/min]; B1='omega e [rad/s]; C1='diametre primitif du pignon; D1='vitesse vremaillère [mm/min]; E1='vitesse vremaillère [mm/s]; A2=36; B2==pi * A2 / 30; C2==InvoluteGear.Modules * InvoluteGear.NumberOfTeeth; D2==B2 * C2 / 2; E2==D2 / 60; A3=100; B3==pi * A3 / 30; C3==InvoluteGear.Modules * InvoluteGear.NumberOfTeeth; D3==B3 * C3 / 2; E3==D3 / 60; A7='Distance a parcourir
FEATURE [Sketcher::SketchObject] Sketch193
  ArcFitTolerance = 1e-06
  AttachmentOffset = pos=(0,0,5) rot=(0,0,1;0rad)
  AttachmentSupport = -> [XY_Plane269]
  ExternalGeometry = -> [BaseFeature002]
  FullyConstrained = true
  MakeInternals = false
  MapMode = 5
  Placement = pos=(0,0,5) rot=(0,0,1;0rad)
  sketch-geometry (4):
    g0: LineSegment StartX=-18.5 StartY=-3.14159 StartZ=0 EndX=-6.5 EndY=-3.14159 EndZ=0
    g1: LineSegment StartX=-6.5 StartY=-3.14159 StartZ=0 EndX=-6.5 EndY=153.938 EndZ=0
    g2: LineSegment StartX=-6.5 StartY=153.938 StartZ=0 EndX=-18.5 EndY=153.938 EndZ=0
    g3: LineSegment StartX=-18.5 StartY=153.938 StartZ=0 EndX=-18.5 EndY=-3.14159 EndZ=0
  constraints (10):
    c: Coincident(g0,g1)
    c: Coincident(g1,g2)
    c: Coincident(g2,g3)
    c: Coincident(g3,g0)
    c: Horizontal(g0)
    c: Horizontal(g2)
    c: Vertical(g1)
    c: Distance(g1,g3) = 12
    c: Coincident(g0,g-4)
    c: Coincident(g2,g-3)
FEATURE [Mesh::Feature] open_tin_can
  Placement = pos=(-50,0,0) rot=(-1,0,0;1.5708rad)
FEATURE [Mesh::Feature] open_tin_can001
  Placement = pos=(50,0,0) rot=(-1,0,0;1.5708rad)
FEATURE [App::Part] Part002007  label="canettes"
  Group = -> [open_tin_can,open_tin_can001]
  Origin = -> Origin
  Placement = pos=(0,-100,-17) rot=(0,0,1;0rad)
FEATURE [Sketcher::SketchObject] Sketch194
  ArcFitTolerance = 1e-06
  AttachmentSupport = -> [XZ_Plane270]
  FullyConstrained = true
  MakeInternals = false
  MapMode = 5
  Placement = pos=(0,0,0) rot=(0,0.707107,0.707107;3.14159rad)
  sketch-geometry (17):
    g0: Circle [constr] CenterX=-10 CenterY=10 CenterZ=0 NormalX=0 NormalY=0 NormalZ=1 AngleXU=0 Radius=2
    g1: LineSegment [constr] StartX=-15 StartY=22.5 StartZ=0 EndX=-15 EndY=-22.5 EndZ=0
    g2: LineSegment [constr] StartX=-15 StartY=-22.5 StartZ=0 EndX=15 EndY=-22.5 EndZ=0
    g3: LineSegment [constr] StartX=15 StartY=-22.5 StartZ=0 EndX=15 EndY=22.5 EndZ=0
    g4: LineSegment [constr] StartX=15 StartY=22.5 StartZ=0 EndX=-15 EndY=22.5 EndZ=0
    g5: LineSegment StartX=-60 StartY=30 StartZ=0 EndX=60 EndY=30 EndZ=0
    g6: LineSegment StartX=70 StartY=20 StartZ=0 EndX=70 EndY=-25 EndZ=0
    g7: LineSegment StartX=60 StartY=-35 StartZ=0 EndX=-60 EndY=-35 EndZ=0
    g8: LineSegment StartX=-70 StartY=20 StartZ=0 EndX=-70 EndY=-25 EndZ=0
    g9: ArcOfCircle CenterX=-60 CenterY=20 CenterZ=0 NormalX=0 NormalY=0 NormalZ=1 AngleXU=0 Radius=10 StartAngle=1.5708 EndAngle=3.14159
    g10: GeomPoint [constr] X=-70 Y=30 Z=0
    g11: ArcOfCircle CenterX=-60 CenterY=-25 CenterZ=0 NormalX=0 NormalY=0 NormalZ=1 AngleXU=0 Radius=10 StartAngle=3.14159 EndAngle=4.71239
    g12: GeomPoint [constr] X=-70 Y=-35 Z=0
    g13: ArcOfCircle CenterX=60 CenterY=20 CenterZ=0 NormalX=0 NormalY=0 NormalZ=1 AngleXU=0 Radius=10 StartAngle=0 EndAngle=1.5708
    g14: GeomPoint [constr] X=70 Y=30 Z=0
    g15: ArcOfCircle CenterX=60 CenterY=-25 CenterZ=0 NormalX=0 NormalY=0 NormalZ=1 AngleXU=0 Radius=10 StartAngle=4.71239 EndAngle=6.28319
    g16: GeomPoint [constr] X=70 Y=-35 Z=0
  constraints (41):
    c: Diameter(g0) = 4
    c: DistanceX(g0,g-1) = 10
    c: Distance(g0,g-1) = 10
    c: Coincident(g4,g1)
    c: Vertical(g1)
    c: Vertical(g3)
    c: Horizontal(g2)
    c: Horizontal(g4)
    c: Coincident(g3,g4)
    c: Coincident(g1,g2)
    c: Symmetric(g1,g3,g-1)
    c: DistanceX(g4,g4) = 30
    c: DistanceY(g1,g1) = 45
    c: Vertical(g6)
    c: Horizontal(g7)
    c: Vertical(g8)
    c: Coincident(g2,g3)
    c: Symmetric(g14,g10,g-2)
    c: DistanceY(g16,g-1) = 35
    c: DistanceY(g-1,g14) = 30
    c: DistanceX(g10,g14) = 140
    c: PointOnObject(g10,g5)
    c: PointOnObject(g10,g8)
    c: Tangent(g5,g9) = 1.5708
    c: Tangent(g8,g9) = -1.5708
    c: PointOnObject(g12,g8)
    c: PointOnObject(g12,g7)
    c: Tangent(g8,g11) = -1.5708
    c: Tangent(g7,g11) = 1.5708
    c: PointOnObject(g14,g6)
    c: PointOnObject(g14,g5)
    c: Tangent(g6,g13) = 1.5708
    c: Tangent(g5,g13) = 1.5708
    c: PointOnObject(g16,g6)
    c: PointOnObject(g16,g7)
    c: Tangent(g6,g15) = 1.5708
    c: Tangent(g7,g15) = 1.5708
    c: Equal(g15,g11)
    c: Equal(g11,g9)
    c: Equal(g9,g13)
    c: Radius(g9) = 10
FEATURE [PartDesign::Pad] Pad096
  Direction = (0,1,-2e-16)
  Length = 3
  Length2 = 10
  Placement = pos=(0,0,0) rot=(1,0,0;1.5708rad)
  Profile = -> Sketch194
  ReferenceAxis = -> Sketch194 [N_Axis]
  Suppressed = false
  Type = 0
FEATURE [Sketcher::SketchObject] Sketch195
  ArcFitTolerance = 1e-06
  AttachmentSupport = -> [Pad096]
  FullyConstrained = true
  MakeInternals = false
  MapMode = 5
  Placement = pos=(0,3,0) rot=(-1,0,0;1.5708rad)
  sketch-geometry (1):
    g0: Circle CenterX=10 CenterY=-10 CenterZ=0 NormalX=0 NormalY=0 NormalZ=1 AngleXU=0 Radius=1.5
  constraints (3):
    c: Diameter(g0) = 3
    c: DistanceX(g-1,g0) = 10
    c: DistanceY(g0,g-1) = 10
FEATURE [PartDesign::Pocket] Pocket075  label="fixation_rail"
  BaseFeature = -> Pad096
  Direction = (0,-1,-2e-16)
  Length = 5
  Length2 = 5
  Placement = pos=(0,0,0) rot=(1,0,0;1.5708rad)
  Profile = -> Sketch195
  ReferenceAxis = -> Sketch195 [N_Axis]
  Suppressed = false
  Type = 0
FEATURE [PartDesign::PolarPattern] PolarPattern011
  Angle = 360
  Axis = -> Sketch195 [N_Axis]
  BaseFeature = -> Pocket075
  Mode = 0
  Occurrences = 4
  Offset = 120
  Originals = -> [Pocket075]
  Placement = pos=(0,0,0) rot=(1,0,0;1.5708rad)
  Suppressed = false
  TransformMode = 0
FEATURE [Sketcher::SketchObject] Sketch196
  ArcFitTolerance = 1e-06
  AttachmentOffset = pos=(65,5,0) rot=(0,0,1;0rad)
  AttachmentSupport = -> [PolarPattern011]
  FullyConstrained = true
  MakeInternals = false
  MapMode = 5
  Placement = pos=(65,3,-5) rot=(-1,0,0;1.5708rad)
  sketch-geometry (1):
    g0: Circle CenterX=0 CenterY=0 CenterZ=0 NormalX=0 NormalY=0 NormalZ=1 AngleXU=0 Radius=1.5
  constraints (2):
    c: Diameter(g0) = 3
    c: Coincident(g0,g-1)
FEATURE [PartDesign::Pocket] Pocket076
  BaseFeature = -> PolarPattern011
  Direction = (0,-1,-2e-16)
  Length = 5
  Length2 = 5
  Placement = pos=(0,0,0) rot=(1,0,0;1.5708rad)
  Profile = -> Sketch196
  ReferenceAxis = -> Sketch196 [N_Axis]
  Suppressed = false
  Type = 0
FEATURE [PartDesign::LinearPattern] LinearPattern003
  Direction = -> Sketch196 [H_Axis]
  Length = 40
  Mode = 1
  Occurrences = 5
  Offset = 10
  Placement = pos=(0,0,0) rot=(1,0,0;1.5708rad)
  Reversed = true
  Suppressed = false
  TransformMode = 0
FEATURE [PartDesign::LinearPattern] LinearPattern004
  Direction = -> Sketch196 [V_Axis]
  Length = 20
  Mode = 1
  Occurrences = 3
  Offset = 10
  Placement = pos=(0,0,0) rot=(1,0,0;1.5708rad)
  Suppressed = false
  TransformMode = 0
FEATURE [PartDesign::MultiTransform] MultiTransform
  BaseFeature = -> Pocket076
  Originals = -> [Pocket076]
  Placement = pos=(0,0,0) rot=(1,0,0;1.5708rad)
  Suppressed = false
  TransformMode = 0
  Transformations = -> [LinearPattern003,LinearPattern004]
FEATURE [Sketcher::SketchObject] Sketch197
  ArcFitTolerance = 1e-06
  AttachmentSupport = -> [MultiTransform]
  FullyConstrained = true
  MakeInternals = false
  MapMode = 5
  Placement = pos=(0,3,0) rot=(-1,0,0;1.5708rad)
  sketch-geometry (16):
    g0: Circle CenterX=-66 CenterY=-9 CenterZ=0 NormalX=0 NormalY=0 NormalZ=1 AngleXU=0 Radius=1.5
    g1: Circle CenterX=-66 CenterY=-19 CenterZ=0 NormalX=0 NormalY=0 NormalZ=1 AngleXU=0 Radius=1.5
    g2: Circle CenterX=-15.5 CenterY=-9 CenterZ=0 NormalX=0 NormalY=0 NormalZ=1 AngleXU=0 Radius=1.5
    g3: Circle CenterX=-15.5 CenterY=-19 CenterZ=0 NormalX=0 NormalY=0 NormalZ=1 AngleXU=0 Radius=1.5
    g4: LineSegment [constr] StartX=-61.25 StartY=-4 StartZ=0 EndX=-61.25 EndY=-24 EndZ=0
    g5: LineSegment [constr] StartX=-61.25 StartY=-24 StartZ=0 EndX=-20.25 EndY=-24 EndZ=0
    g6: LineSegment [constr] StartX=-20.25 StartY=-24 StartZ=0 EndX=-20.25 EndY=-4 EndZ=0
    g7: LineSegment [constr] StartX=-20.25 StartY=-4 StartZ=0 EndX=-61.25 EndY=-4 EndZ=0
    g8: LineSegment StartX=-19.25 StartY=-24 StartZ=0 EndX=-19.25 EndY=-4 EndZ=0
    g9: ArcOfCircle CenterX=-20.25 CenterY=-4 CenterZ=0 NormalX=0 NormalY=0 NormalZ=-1 AngleXU=0 Radius=1 StartAngle=1.5708 EndAngle=3.14159
    g10: LineSegment StartX=-20.25 StartY=-3 StartZ=0 EndX=-61.25 EndY=-3 EndZ=0
    g11: ArcOfCircle CenterX=-61.25 CenterY=-4 CenterZ=0 NormalX=0 NormalY=0 NormalZ=-1 AngleXU=0 Radius=1 StartAngle=-1.8e-15 EndAngle=1.5708
    g12: LineSegment StartX=-62.25 StartY=-4 StartZ=0 EndX=-62.25 EndY=-24 EndZ=0
    g13: ArcOfCircle CenterX=-61.25 CenterY=-24 CenterZ=0 NormalX=0 NormalY=0 NormalZ=-1 AngleXU=0 Radius=1 StartAngle=4.71239 EndAngle=6.28319
    g14: LineSegment StartX=-61.25 StartY=-25 StartZ=0 EndX=-20.25 EndY=-25 EndZ=0
    g15: ArcOfCircle CenterX=-20.25 CenterY=-24 CenterZ=0 NormalX=0 NormalY=0 NormalZ=-1 AngleXU=0 Radius=1 StartAngle=3.14159 EndAngle=4.71239
  constraints (40):
    c: Vertical(g2,g3)
    c: Vertical(g0,g1)
    c: Horizontal(g0,g2)
    c: Horizontal(g1,g3)
    c: Equal(g0,g1)
    c: Equal(g1,g2)
    c: Equal(g2,g3)
    c: Diameter(g2) = 3
    c: DistanceY(g3,g2) = 10
    c: DistanceX(g1,g3) = 50.5
    c: DistanceY(g3,g-1) = 19
    c: DistanceX(g3,g-1) = 15.5
    c: Coincident(g4,g5)
    c: Coincident(g5,g6)
    c: Coincident(g6,g7)
    c: Coincident(g7,g4)
    c: Vertical(g4)
    c: Vertical(g6)
    c: Horizontal(g5)
    c: Horizontal(g7)
    c: DistanceX(g7,g7) = 41
    c: DistanceY(g4,g4) = 20
    c: Tangent(g8,g9) = -1.5708
    c: Tangent(g8,g15) = -1.5708
    c: Tangent(g9,g10) = -1.5708
    c: Tangent(g10,g11) = -1.5708
    c: Tangent(g11,g12) = -1.5708
    c: Tangent(g12,g13) = -1.5708
    c: Tangent(g14,g15) = -1.5708
    c: Coincident(g4,g11)
    c: Coincident(g6,g9)
    c: Coincident(g5,g15)
    c: Coincident(g4,g13)
    c: Horizontal(g10)
    c: Vertical(g12)
    c: Vertical(g8)
    c: Radius(g9) = 1
    c: DistanceY(g6,g-1) = 4
    c: DistanceX(g6,g-1) = 20.25
    c: Tangent(g14,g13) = -1.5708
FEATURE [PartDesign::Pocket] Pocket077  label="fixation_servo"
  BaseFeature = -> MultiTransform
  Direction = (0,-1,-2e-16)
  Length = 5
  Length2 = 5
  Placement = pos=(0,0,0) rot=(1,0,0;1.5708rad)
  Profile = -> Sketch197
  ReferenceAxis = -> Sketch197 [N_Axis]
  Suppressed = false
  Type = 0
FEATURE [Sketcher::SketchObject] Sketch198
  ArcFitTolerance = 1e-06
  AttachmentSupport = -> [XY_Plane271]
  FullyConstrained = true
  MakeInternals = false
  MapMode = 5
  sketch-geometry (6):
    g0: ArcOfCircle CenterX=-5 CenterY=0 CenterZ=0 NormalX=0 NormalY=0 NormalZ=1 AngleXU=0 Radius=3 StartAngle=1.5708 EndAngle=4.71239
    g1: ArcOfCircle CenterX=5 CenterY=0 CenterZ=0 NormalX=0 NormalY=0 NormalZ=1 AngleXU=0 Radius=3 StartAngle=4.71239 EndAngle=7.85398
    g2: LineSegment StartX=-5 StartY=3 StartZ=0 EndX=5 EndY=3 EndZ=0
    g3: LineSegment StartX=-5 StartY=-3 StartZ=0 EndX=5 EndY=-3 EndZ=0
    g4: Circle CenterX=-5 CenterY=0 CenterZ=0 NormalX=0 NormalY=0 NormalZ=1 AngleXU=0 Radius=2
    g5: Circle CenterX=5 CenterY=0 CenterZ=0 NormalX=0 NormalY=0 NormalZ=1 AngleXU=0 Radius=2
  constraints (13):
    c: Tangent(g0,g2) = 1.5708
    c: Tangent(g0,g3) = -1.5708
    c: Tangent(g1,g2) = 1.5708
    c: Tangent(g1,g3) = -1.5708
    c: Equal(g0,g1)
    c: Horizontal(g3)
    c: Symmetric(g0,g1,g-1)
    c: DistanceX(g0,g1) = 10
    c: Radius(g0) = 3
    c: Coincident(g4,g0)
    c: Coincident(g5,g1)
    c: Equal(g5,g4)
    c: Diameter(g4) = 4
FEATURE [PartDesign::Pad] Pad097
  Direction = (0,0,1)
  Length = 10.9
  Length2 = 10
  Profile = -> Sketch198
  ReferenceAxis = -> Sketch198 [N_Axis]
  Suppressed = false
  Type = 0
FEATURE [Sketcher::SketchObject] Sketch199
  ArcFitTolerance = 1e-06
  AttachmentSupport = -> [XY_Plane272]
  FullyConstrained = true
  MakeInternals = false
  MapMode = 5
  sketch-geometry (6):
    g0: ArcOfCircle CenterX=-5 CenterY=0 CenterZ=0 NormalX=0 NormalY=0 NormalZ=1 AngleXU=0 Radius=3.5 StartAngle=1.5708 EndAngle=4.71239
    g1: ArcOfCircle CenterX=5 CenterY=0 CenterZ=0 NormalX=0 NormalY=0 NormalZ=1 AngleXU=0 Radius=3.5 StartAngle=4.71239 EndAngle=7.85398
    g2: LineSegment StartX=-5 StartY=3.5 StartZ=0 EndX=5 EndY=3.5 EndZ=0
    g3: LineSegment StartX=-5 StartY=-3.5 StartZ=0 EndX=5 EndY=-3.5 EndZ=0
    g4: Circle CenterX=-5 CenterY=0 CenterZ=0 NormalX=0 NormalY=0 NormalZ=1 AngleXU=0 Radius=2.8
    g5: Circle CenterX=5 CenterY=0 CenterZ=0 NormalX=0 NormalY=0 NormalZ=1 AngleXU=0 Radius=2.8
  constraints (13):
    c: Tangent(g0,g2) = 1.5708
    c: Tangent(g0,g3) = -1.5708
    c: Tangent(g1,g2) = 1.5708
    c: Tangent(g1,g3) = -1.5708
    c: Equal(g0,g1)
    c: Horizontal(g3)
    c: Symmetric(g0,g1,g-1)
    c: DistanceX(g0,g1) = 10
    c: Radius(g0) = 3.5
    c: Coincident(g4,g0)
    c: Coincident(g5,g1)
    c: Equal(g5,g4)
    c: Diameter(g4) = 5.6
FEATURE [PartDesign::Pad] Pad098
  Direction = (0,0,1)
  Length = 1
  Length2 = 10
  Profile = -> Sketch199
  ReferenceAxis = -> Sketch199 [N_Axis]
  Suppressed = false
  Type = 0
FEATURE [PartDesign::Body] Body076  label="DA20_insert"
  AllowCompound = false
  Group = -> [Sketch199,Pad098]
  Origin = -> Origin275
  Placement = pos=(0,-6,35) rot=(0,-0.707107,0.707107;3.14159rad)
  Tip = -> Pad098
FEATURE [Part::FeaturePython] Nut  label="M5-Écrou"  # WARN: FeaturePython — macro-defined, semantics opaque (R4)
  Diameter = 10
  Invert = false
  LeftHanded = false
  MatchOuter = false
  OffsetAngle = 0
  Placement = pos=(-5,11.5,35) rot=(1,0,0;1.5708rad)
  Thread = false
  Type = 19
FEATURE [Part::FeaturePython] Screw  label="M3x10-Vis"  # WARN: FeaturePython — macro-defined, semantics opaque (R4)
  Diameter = 3
  Invert = false
  LeftHanded = false
  Length = 3
  LengthCustom = 10
  MatchOuter = false
  OffsetAngle = 0
  Thread = false
  Type = 52
FEATURE [App::VarSet] VarSet
  Position_elevateur_canette = 124
FEATURE [App::LinkElement] Link_i0
  LinkPlacement = pos=(-4.37114e-07,-7.62939e-06,-5) rot=(0,1,0;3.14159rad)
  LinkedObject = -> <external CanaPince.FCStd>#Part004
  Placement = pos=(-4.37114e-07,-7.62939e-06,-5) rot=(0,1,0;3.14159rad)
  _LinkOwner = 547
FEATURE [App::LinkElement] Link_i1
  LinkPlacement = pos=(100,-8.39233e-05,25.0001) rot=(0,1.00347,0;0rad)
  LinkedObject = -> <external CanaPince.FCStd>#Part004
  Placement = pos=(100,-8.39233e-05,25.0001) rot=(0,1.00347,0;0rad)
  _LinkOwner = 547
FEATURE [App::Link] Link  label="CanaPince_Servomoteur"
  ElementCount = 2
  ElementList = -> [Link_i0,Link_i1]
  LinkPlacement = pos=(14,-50,100) rot=(0.57735,0.57735,0.57735;2.0944rad)
  LinkedObject = -> <external CanaPince.FCStd>#Part004
  Placement = pos=(14,-50,100) rot=(0.57735,0.57735,0.57735;2.0944rad)
FEATURE [Sketcher::SketchObject] Sketch206
  ArcFitTolerance = 1e-06
  AttachmentOffset = pos=(50,11.5,0) rot=(0,0,1;0rad)
  AttachmentSupport = -> [XZ_Plane270]
  FullyConstrained = true
  MakeInternals = false
  MapMode = 5
  Placement = pos=(50,2.6e-15,11.5) rot=(1,0,0;1.5708rad)
  sketch-geometry (1):
    g0: Circle CenterX=15 CenterY=4 CenterZ=0 NormalX=0 NormalY=0 NormalZ=1 AngleXU=0 Radius=1.5
  constraints (3):
    c: Diameter(g0) = 3
    c: DistanceX(g-1,g0) = 15
    c: DistanceY(g-1,g0) = 4
FEATURE [PartDesign::Pocket] Pocket081  label="support_pince_d"
  BaseFeature = -> Pocket077
  Direction = (0,1,-2e-16)
  Length = 5
  Length2 = 5
  Placement = pos=(0,0,0) rot=(1,0,0;1.5708rad)
  Profile = -> Sketch206
  ReferenceAxis = -> Sketch206 [N_Axis]
  Suppressed = false
  Type = 1
FEATURE [PartDesign::Mirrored] Mirrored001
  MirrorPlane = -> Sketch206 [V_Axis]
  Placement = pos=(0,0,0) rot=(1,0,0;1.5708rad)
  Suppressed = false
  TransformMode = 0
FEATURE [PartDesign::Mirrored] Mirrored002
  MirrorPlane = -> Sketch206 [H_Axis]
  Placement = pos=(0,0,0) rot=(1,0,0;1.5708rad)
  Suppressed = false
  TransformMode = 0
FEATURE [PartDesign::MultiTransform] MultiTransform001
  BaseFeature = -> Pocket081
  Originals = -> [Pocket081]
  Placement = pos=(0,0,0) rot=(1,0,0;1.5708rad)
  Suppressed = false
  TransformMode = 0
  Transformations = -> [Mirrored001,Mirrored002]
FEATURE [Sketcher::SketchObject] Sketch207
  ArcFitTolerance = 1e-06
  AttachmentOffset = pos=(-50,-13.5,0) rot=(0,0,1;0rad)
  AttachmentSupport = -> [XZ_Plane270]
  FullyConstrained = true
  MakeInternals = false
  MapMode = 5
  Placement = pos=(-50,-3e-15,-13.5) rot=(1,0,0;1.5708rad)
  sketch-geometry (1):
    g0: Circle CenterX=15 CenterY=4 CenterZ=0 NormalX=0 NormalY=0 NormalZ=1 AngleXU=0 Radius=1.5
  constraints (3):
    c: Diameter(g0) = 3
    c: DistanceX(g-1,g0) = 15
    c: DistanceY(g-1,g0) = 4
FEATURE [PartDesign::Pocket] Pocket082
  BaseFeature = -> MultiTransform001
  Direction = (0,1,-2e-16)
  Length = 5
  Length2 = 5
  Placement = pos=(0,0,0) rot=(1,0,0;1.5708rad)
  Profile = -> Sketch207
  ReferenceAxis = -> Sketch207 [N_Axis]
  Suppressed = false
  Type = 0
FEATURE [PartDesign::Mirrored] Mirrored003
  MirrorPlane = -> Sketch207 [V_Axis]
  Placement = pos=(0,0,0) rot=(1,0,0;1.5708rad)
  Suppressed = false
  TransformMode = 0
FEATURE [PartDesign::Mirrored] Mirrored004
  MirrorPlane = -> Sketch207 [H_Axis]
  Placement = pos=(0,0,0) rot=(1,0,0;1.5708rad)
  Suppressed = false
  TransformMode = 0
FEATURE [PartDesign::MultiTransform] MultiTransform002
  BaseFeature = -> Pocket082
  Originals = -> [Pocket082]
  Placement = pos=(0,0,0) rot=(1,0,0;1.5708rad)
  Suppressed = false
  TransformMode = 0
  Transformations = -> [Mirrored003,Mirrored004]
FEATURE [Sketcher::SketchObject] Sketch208
  ArcFitTolerance = 1e-06
  AttachmentSupport = -> [YZ_Plane274]
  FullyConstrained = true
  MakeInternals = false
  MapMode = 5
  Placement = pos=(0,0,0) rot=(0.57735,0.57735,0.57735;2.0944rad)
  sketch-geometry (14):
    g0: LineSegment StartX=-6.075 StartY=4.075 StartZ=0 EndX=-6.075 EndY=-4.075 EndZ=0
    g1: LineSegment StartX=-6.075 StartY=-4.075 StartZ=0 EndX=6.075 EndY=-4.075 EndZ=0
    g2: LineSegment StartX=6.075 StartY=-4.075 StartZ=0 EndX=6.075 EndY=4.075 EndZ=0
    g3: LineSegment StartX=6.075 StartY=4.075 StartZ=0 EndX=-6.075 EndY=4.075 EndZ=0
    g4: LineSegment StartX=-10.075 StartY=4.075 StartZ=0 EndX=-10.075 EndY=-5.075 EndZ=0
    g5: LineSegment StartX=-7.075 StartY=-8.075 StartZ=0 EndX=7.075 EndY=-8.075 EndZ=0
    g6: LineSegment StartX=10.075 StartY=-5.075 StartZ=0 EndX=10.075 EndY=4.075 EndZ=0
    g7: LineSegment StartX=7.075 StartY=7.075 StartZ=0 EndX=-7.075 EndY=7.075 EndZ=0
    g8: ArcOfCircle CenterX=-7.075 CenterY=4.075 CenterZ=0 NormalX=0 NormalY=0 NormalZ=1 AngleXU=0 Radius=3 StartAngle=1.5708 EndAngle=3.14159
    g9: ArcOfCircle CenterX=-7.075 CenterY=-5.075 CenterZ=0 NormalX=0 NormalY=0 NormalZ=1 AngleXU=0 Radius=3 StartAngle=3.14159 EndAngle=4.71239
    g10: ArcOfCircle CenterX=7.075 CenterY=-5.075 CenterZ=0 NormalX=0 NormalY=0 NormalZ=1 AngleXU=0 Radius=3 StartAngle=4.71239 EndAngle=6.28319
    g11: ArcOfCircle CenterX=7.075 CenterY=4.075 CenterZ=0 NormalX=0 NormalY=0 NormalZ=1 AngleXU=0 Radius=3 StartAngle=0 EndAngle=1.5708
    g12: GeomPoint [constr] X=-10.075 Y=7.075 Z=0
    g13: GeomPoint [constr] X=10.075 Y=-8.075 Z=0
  constraints (34):
    c: Coincident(g0,g1)
    c: Coincident(g1,g2)
    c: Coincident(g2,g3)
    c: Coincident(g3,g0)
    c: Vertical(g0)
    c: Vertical(g2)
    c: Horizontal(g1)
    c: Horizontal(g3)
    c: Symmetric(g2,g0,g-1)
    c: DistanceX(g3,g3) = 12.15
    c: DistanceY(g0,g0) = 8.15
    c: Tangent(g4,g8) = -1.5708
    c: Tangent(g4,g9) = -1.5708
    c: Tangent(g5,g9) = -1.5708
    c: Tangent(g5,g10) = -1.5708
    c: Tangent(g6,g10) = -1.5708
    c: Tangent(g6,g11) = -1.5708
    c: Tangent(g7,g11) = -1.5708
    c: Tangent(g7,g8) = -1.5708
    c: Vertical(g4)
    c: Vertical(g6)
    c: Horizontal(g5)
    c: Horizontal(g7)
    c: Equal(g8,g9)
    c: Equal(g9,g10)
    c: PointOnObject(g12,g4)
    c: PointOnObject(g12,g7)
    c: PointOnObject(g13,g5)
    c: PointOnObject(g13,g6)
    c: Radius(g9) = 3
    c: Symmetric(g11,g8,g-2)
    c: DistanceX(g4,g0) = 4
    c: DistanceY(g0,g7) = 3
    c: DistanceY(g5,g0) = 4
FEATURE [PartDesign::Pad] Pad102
  Direction = (1,0,0)
  Length = 10
  Length2 = 2
  Placement = pos=(0,0,0) rot=(1,1,1;2.0944rad)
  Profile = -> Sketch208
  ReferenceAxis = -> Sketch208 [N_Axis]
  Suppressed = false
  Type = 4
FEATURE [Sketcher::SketchObject] Sketch209
  ArcFitTolerance = 1e-06
  AttachmentSupport = -> [Pad102]
  ExternalGeometry = -> [Pad102]
  FullyConstrained = true
  MakeInternals = false
  MapMode = 5
  Placement = pos=(-2,0,0) rot=(0.57735,0.57735,-0.57735;4.18879rad)
  sketch-geometry (4):
    g0: LineSegment StartX=-6.075 StartY=4.075 StartZ=0 EndX=-6.075 EndY=-4.075 EndZ=0
    g1: LineSegment StartX=-6.075 StartY=-4.075 StartZ=0 EndX=6.075 EndY=-4.075 EndZ=0
    g2: LineSegment StartX=6.075 StartY=-4.075 StartZ=0 EndX=6.075 EndY=4.075 EndZ=0
    g3: LineSegment StartX=6.075 StartY=4.075 StartZ=0 EndX=-6.075 EndY=4.075 EndZ=0
  constraints (10):
    c: Coincident(g0,g1)
    c: Coincident(g1,g2)
    c: Coincident(g2,g3)
    c: Coincident(g3,g0)
    c: Vertical(g0)
    c: Vertical(g2)
    c: Horizontal(g1)
    c: Horizontal(g3)
    c: Coincident(g0,g-3)
    c: Coincident(g1,g-4)
FEATURE [PartDesign::Pad] Pad103
  BaseFeature = -> Pad102
  Direction = (-1,0,0)
  Length = 2
  Length2 = 10
  Placement = pos=(0,0,0) rot=(1,1,1;2.0944rad)
  Profile = -> Sketch209
  ReferenceAxis = -> Sketch209 [N_Axis]
  Refine = true
  Reversed = true
  Suppressed = false
  Type = 0
FEATURE [Sketcher::SketchObject] Sketch210
  ArcFitTolerance = 1e-06
  AttachmentSupport = -> [Pad103]
  ExternalGeometry = -> [Pad103]
  FullyConstrained = true
  MakeInternals = false
  MapMode = 5
  Placement = pos=(-2,0,-1.1e-15) rot=(0.57735,0.57735,-0.57735;4.18879rad)
  sketch-geometry (11):
    g0: ArcOfCircle CenterX=-28 CenterY=1.8 CenterZ=0 NormalX=0 NormalY=0 NormalZ=1 AngleXU=0 Radius=3 StartAngle=1.7489 EndAngle=4.71239
    g1: ArcOfCircle CenterX=-6.8 CenterY=23 CenterZ=0 NormalX=0 NormalY=0 NormalZ=1 AngleXU=0 Radius=3 StartAngle=2e-16 EndAngle=3.1232
    g2: LineSegment StartX=-28.5315 StartY=4.75254 StartZ=0 EndX=-18.1507 EndY=6.62124 EndZ=0
    g3: LineSegment StartX=-28 StartY=-1.2 StartZ=0 EndX=-10.075 EndY=-1.2 EndZ=0
    g4: LineSegment StartX=-9.79949 StartY=23.0552 StartZ=0 EndX=-9.92411 EndY=16.2792 EndZ=0
    g5: LineSegment StartX=-3.8 StartY=23 StartZ=0 EndX=-3.8 EndY=8.075 EndZ=0
    g6: LineSegment StartX=-10.075 StartY=-1.2 StartZ=0 EndX=-3.8 EndY=8.075 EndZ=0
    g7: Circle CenterX=-6.8 CenterY=23 CenterZ=0 NormalX=0 NormalY=0 NormalZ=1 AngleXU=0 Radius=1.75
    g8: Circle CenterX=-28 CenterY=1.8 CenterZ=0 NormalX=0 NormalY=0 NormalZ=1 AngleXU=0 Radius=1.75
    g9: ArcOfCircle CenterX=-19.9224 CenterY=16.463 CenterZ=0 NormalX=0 NormalY=0 NormalZ=1 AngleXU=0 Radius=10 StartAngle=4.8905 EndAngle=6.2648
    g10: GeomPoint [constr] X=-10.075 Y=8.075 Z=0
  constraints (27):
    c: Coincident(g6,g5)
    c: PointOnObject(g5,g-3)
    c: Tangent(g5,g1) = 1.5708
    c: Tangent(g4,g1) = -1.5708
    c: Tangent(g2,g0) = 1.5708
    c: Tangent(g3,g0) = -1.5708
    c: PointOnObject(g3,g-4)
    c: PointOnObject(g10,g-4)
    c: Diameter(g7) = 3.5
    c: Coincident(g7,g1)
    c: Coincident(g8,g0)
    c: Equal(g8,g7)
    c: Equal(g0,g1)
    c: Radius(g1) = 3
    c: DistanceX(g0,g-1) = 28
    c: DistanceY(g-1,g1) = 23
    c: DistanceX(g1,g-1) = 6.8
    c: Coincident(g3,g6)
    c: PointOnObject(g10,g4)
    c: PointOnObject(g10,g2)
    c: Tangent(g4,g9) = 1.5708
    c: Tangent(g2,g9) = -1.5708
    c: Radius(g9) = 10
    c: PointOnObject(g10,g-3)
    c: Horizontal(g3)
    c: Vertical(g5)
    c: DistanceY(g-1,g0) = 1.8
FEATURE [PartDesign::Pad] Pad104
  BaseFeature = -> Pad103
  Direction = (-1,0,0)
  Length = 4
  Length2 = 10
  Placement = pos=(0,0,0) rot=(1,1,1;2.0944rad)
  Profile = -> Sketch210
  ReferenceAxis = -> Sketch210 [N_Axis]
  Refine = true
  Reversed = true
  Suppressed = false
  Type = 0
FEATURE [PartDesign::Fillet] Fillet
  Base = -> Pad104 [Edge11]
  BaseFeature = -> Pad104
  Placement = pos=(0,0,0) rot=(1,1,1;2.0944rad)
  Radius = 3
  SupportTransform = false
  Suppressed = false
  UseAllEdges = false
FEATURE [PartDesign::Mirrored] Mirrored005
  BaseFeature = -> Fillet
  MirrorPlane = -> Sketch210 [V_Axis]
  Originals = -> [Pad104,Fillet]
  Placement = pos=(0,0,0) rot=(1,1,1;2.0944rad)
  Refine = true
  Suppressed = false
  TransformMode = 0
FEATURE [Sketcher::SketchObject] Sketch211
  ArcFitTolerance = 1e-06
  AttachmentSupport = -> [XY_Plane274]
  FullyConstrained = true
  MakeInternals = false
  MapMode = 5
  expr: Constraints[0] = 3.7
  sketch-geometry (1):
    g0: Circle CenterX=10 CenterY=0 CenterZ=0 NormalX=0 NormalY=0 NormalZ=1 AngleXU=0 Radius=1.85
  constraints (3):
    c: Diameter(g0) = 3.7
    c: PointOnObject(g0,g-1)
    c: DistanceX(g-1,g0) = 10
FEATURE [PartDesign::Pocket] Pocket083
  BaseFeature = -> Mirrored005
  Direction = (0,0,-1)
  Length = 5
  Length2 = 5
  Placement = pos=(0,0,0) rot=(1,1,1;2.0944rad)
  Profile = -> Sketch211
  ReferenceAxis = -> Sketch211 [N_Axis]
  Suppressed = false
  Type = 1
FEATURE [Sketcher::SketchObject] Sketch212
  ArcFitTolerance = 1e-06
  AttachmentOffset = pos=(0,0,-4.1) rot=(0,0,1;0rad)
  AttachmentSupport = -> [XY_Plane274]
  ExternalGeometry = -> [Pocket083]
  FullyConstrained = true
  MakeInternals = false
  MapMode = 5
  Placement = pos=(0,0,-4.1) rot=(0,0,1;0rad)
  sketch-geometry (8):
    g0: LineSegment StartX=4.15 StartY=6 StartZ=0 EndX=35 EndY=6 EndZ=0
    g1: ArcOfCircle CenterX=35 CenterY=0 CenterZ=0 NormalX=0 NormalY=0 NormalZ=1 AngleXU=0 Radius=6 StartAngle=0 EndAngle=1.5708
    g2: ArcOfCircle CenterX=10 CenterY=-4.9e-15 CenterZ=0 NormalX=0 NormalY=0 NormalZ=1 AngleXU=0 Radius=1.85 StartAngle=2.7e-15 EndAngle=3.14159
    g3: LineSegment StartX=41 StartY=0 StartZ=0 EndX=36.85 EndY=0 EndZ=0
    g4: LineSegment StartX=33.15 StartY=2e-16 StartZ=0 EndX=11.85 EndY=1e-16 EndZ=0
    g5: LineSegment StartX=4.15 StartY=6 StartZ=0 EndX=4.15 EndY=0 EndZ=0
    g6: ArcOfCircle CenterX=35 CenterY=0 CenterZ=0 NormalX=0 NormalY=0 NormalZ=1 AngleXU=0 Radius=1.85 StartAngle=0 EndAngle=3.14159
    g7: LineSegment StartX=4.15 StartY=3e-16 StartZ=0 EndX=8.15 EndY=3e-16 EndZ=0
  constraints (24):
    c: Horizontal(g0)
    c: PointOnObject(g1,g-1)
    c: PointOnObject(g1,g-1)
    c: Tangent(g1,g0) = 1.5708
    c: DistanceX(g-1,g1) = 35
    c: DistanceY(g-1,g0) = 6
    c: Coincident(g2,g-4)
    c: PointOnObject(g2,g-1)
    c: Coincident(g3,g1)
    c: PointOnObject(g3,g-1)
    c: PointOnObject(g4,g-1)
    c: Coincident(g5,g0)
    c: Coincident(g6,g1)
    c: Coincident(g6,g3)
    c: Coincident(g4,g6)
    c: Equal(g6,g2)
    c: Coincident(g2,g4)
    c: Coincident(g7,g5)
    c: Coincident(g7,g2)
    c: Vertical(g5)
    c: Horizontal(g7)
    c: PointOnObject(g2,g-1)
    c: PointOnObject(g2,g-4)
    c: DistanceX(g7,g7) = 4
FEATURE [PartDesign::Pad] Pad105
  BaseFeature = -> Pocket083
  Direction = (0,0,1)
  Length = 6
  Length2 = 10
  Placement = pos=(0,0,0) rot=(1,1,1;2.0944rad)
  Profile = -> Sketch212
  ReferenceAxis = -> Sketch212 [N_Axis]
  Reversed = true
  Suppressed = false
  Type = 0
FEATURE [PartDesign::Chamfer] Chamfer
  Angle = 45
  Base = -> Pad105 [Edge132]
  BaseFeature = -> Pad105
  ChamferType = 0
  FlipDirection = false
  Placement = pos=(0,0,0) rot=(1,1,1;2.0944rad)
  Size = 2
  Size2 = 1
  SupportTransform = false
  Suppressed = false
  UseAllEdges = false
FEATURE [PartDesign::Mirrored] Mirrored006
  BaseFeature = -> Chamfer
  MirrorPlane = -> XZ_Plane274
  Originals = -> [Pad105,Chamfer]
  Placement = pos=(0,0,0) rot=(1,1,1;2.0944rad)
  Refine = true
  Suppressed = false
  TransformMode = 0
FEATURE [Sketcher::SketchObject] Sketch213
  ArcFitTolerance = 1e-06
  AttachmentSupport = -> [XY_Plane274]
  ExternalGeometry = -> [Mirrored006]
  FullyConstrained = true
  MakeInternals = false
  MapMode = 5
  sketch-geometry (1):
    g0: Circle CenterX=10 CenterY=0 CenterZ=0 NormalX=0 NormalY=0 NormalZ=1 AngleXU=0 Radius=3
  constraints (2):
    c: Diameter(g0) = 6
    c: Coincident(g0,g-3)
FEATURE [PartDesign::Pocket] Pocket084
  BaseFeature = -> Mirrored006
  Direction = (0,0,-1)
  Length = 5
  Length2 = 5
  Placement = pos=(0,0,0) rot=(1,1,1;2.0944rad)
  Profile = -> Sketch213
  ReferenceAxis = -> Sketch213 [N_Axis]
  Reversed = true
  Suppressed = false
  Type = 1
FEATURE [Sketcher::SketchObject] Sketch214
  ArcFitTolerance = 1e-06
  AttachmentSupport = -> [XZ_Plane275]
  FullyConstrained = true
  MakeInternals = false
  MapMode = 5
  Placement = pos=(0,0,0) rot=(1,0,0;1.5708rad)
  sketch-geometry (6):
    g0: LineSegment StartX=-10 StartY=0 StartZ=0 EndX=0 EndY=0 EndZ=0
    g1: LineSegment StartX=-10 StartY=0 StartZ=0 EndX=-10 EndY=-4 EndZ=0
    g2: LineSegment StartX=-8 StartY=-6 StartZ=0 EndX=0 EndY=-6 EndZ=0
    g3: ArcOfCircle CenterX=-8 CenterY=-4 CenterZ=0 NormalX=0 NormalY=0 NormalZ=1 AngleXU=0 Radius=2 StartAngle=3.14159 EndAngle=4.71239
    g4: GeomPoint [constr] X=-10 Y=-6 Z=0
    g5: LineSegment StartX=0 StartY=-6 StartZ=0 EndX=0 EndY=0 EndZ=0
  constraints (15):
    c: Coincident(g0,g-1)
    c: Horizontal(g0)
    c: Coincident(g0,g1)
    c: Horizontal(g2)
    c: Vertical(g1)
    c: PointOnObject(g4,g1)
    c: PointOnObject(g4,g2)
    c: Tangent(g1,g3) = -1.5708
    c: Tangent(g2,g3) = -1.5708
    c: Radius(g3) = 2
    c: DistanceY(g1,g1) = 4
    c: Coincident(g5,g0)
    c: Vertical(g5)
    c: Coincident(g2,g5)
    c: DistanceX(g1,g-1) = 10
FEATURE [PartDesign::Pad] Pad106
  Direction = (0,-1,2e-16)
  Length = 6
  Length2 = 10
  Midplane = true
  Placement = pos=(0,0,0) rot=(1,0,0;1.5708rad)
  Profile = -> Sketch214
  ReferenceAxis = -> Sketch214 [N_Axis]
  Suppressed = false
  Type = 0
FEATURE [Sketcher::SketchObject] Sketch216
  ArcFitTolerance = 1e-06
  AttachmentSupport = -> [Pad106]
  FullyConstrained = true
  MakeInternals = false
  MapMode = 5
  Placement = pos=(0,-2.6e-15,-6) rot=(1,0,0;3.14159rad)
  sketch-geometry (1):
    g0: Circle CenterX=-5 CenterY=0 CenterZ=0 NormalX=0 NormalY=0 NormalZ=1 AngleXU=0 Radius=2.1
  constraints (3):
    c: Diameter(g0) = 4.2
    c: DistanceX(g0,g-1) = 5
    c: PointOnObject(g0,g-1)
FEATURE [PartDesign::Pocket] Pocket086
  BaseFeature = -> Pad106
  Direction = (0,0,1)
  Length = 6
  Length2 = 5
  Placement = pos=(0,0,0) rot=(1,0,0;1.5708rad)
  Profile = -> Sketch216
  ReferenceAxis = -> Sketch216 [N_Axis]
  Suppressed = false
  Type = 0
FEATURE [Sketcher::SketchObject] Sketch220
  ArcFitTolerance = 1e-06
  AttachmentOffset = pos=(18,0,0) rot=(0,0,1;0rad)
  AttachmentSupport = -> [XZ_Plane270]
  FullyConstrained = true
  MakeInternals = false
  MapMode = 5
  Placement = pos=(18,0,0) rot=(1,0,0;1.5708rad)
  sketch-geometry (2):
    g0: Circle CenterX=0 CenterY=9 CenterZ=0 NormalX=0 NormalY=0 NormalZ=1 AngleXU=0 Radius=1.5
    g1: Circle CenterX=0 CenterY=-9 CenterZ=0 NormalX=0 NormalY=0 NormalZ=1 AngleXU=0 Radius=1.5
  constraints (5):
    c: PointOnObject(g0,g-2)
    c: Equal(g1,g0)
    c: Symmetric(g0,g1,g-1)
    c: DistanceY(g-1,g0) = 9
    c: Diameter(g0) = 3
FEATURE [PartDesign::Pocket] Pocket089
  BaseFeature = -> MultiTransform002
  Direction = (0,1,-2e-16)
  Length = 5
  Length2 = 5
  Placement = pos=(0,0,0) rot=(1,0,0;1.5708rad)
  Profile = -> Sketch220
  ReferenceAxis = -> Sketch220 [N_Axis]
  Suppressed = false
  Type = 0
FEATURE [PartDesign::Body] Body074  label="Plaque_interface"
  AllowCompound = false
  Group = -> [Sketch194,Pad096,Sketch195,Pocket075,PolarPattern011,Sketch196,Pocket076,MultiTransform,LinearPattern003,LinearPattern004,Sketch197,Pocket077,Sketch206,Pocket081,MultiTransform001,Mirrored001,Mirrored002,Sketch207,Pocket082,MultiTransform002,Mirrored003,Mirrored004,Sketch220,Pocket089]
  Origin = -> Origin273
  Placement = pos=(25,-2.9e-15,13) rot=(0.57735,0.57735,0.57735;2.0944rad)
  Tip = -> Pocket089
FEATURE [Sketcher::SketchObject] Sketch221
  ArcFitTolerance = 1e-06
  AttachmentSupport = -> [YZ_Plane276]
  FullyConstrained = true
  MakeInternals = false
  MapMode = 5
  Placement = pos=(0,0,0) rot=(0.57735,0.57735,0.57735;2.0944rad)
  sketch-geometry (1):
    g0: Circle CenterX=0 CenterY=0 CenterZ=0 NormalX=0 NormalY=0 NormalZ=1 AngleXU=0 Radius=1
  constraints (2):
    c: Diameter(g0) = 2
    c: Coincident(g0,g-1)
FEATURE [PartDesign::Pad] Pad108
  Direction = (1,0,0)
  Length = 7
  Length2 = 10
  Placement = pos=(0,0,0) rot=(1,1,1;2.0944rad)
  Profile = -> Sketch221
  ReferenceAxis = -> Sketch221 [N_Axis]
  Suppressed = false
  Type = 0
FEATURE [Sketcher::SketchObject] Sketch222
  ArcFitTolerance = 1e-06
  AttachmentSupport = -> [Pad108]
  FullyConstrained = true
  MakeInternals = false
  MapMode = 5
  Placement = pos=(7,0,0) rot=(0.57735,0.57735,0.57735;2.0944rad)
  sketch-geometry (1):
    g0: Circle CenterX=0 CenterY=0 CenterZ=0 NormalX=0 NormalY=0 NormalZ=1 AngleXU=0 Radius=0.25
  constraints (2):
    c: Diameter(g0) = 0.5
    c: Coincident(g0,g-1)
FEATURE [Sketcher::SketchObject] Sketch223
  ArcFitTolerance = 1e-06
  AttachmentSupport = -> [XZ_Plane276]
  ExternalGeometry = -> [Pad108]
  FullyConstrained = true
  MakeInternals = false
  MapMode = 5
  Placement = pos=(0,0,0) rot=(1,0,0;1.5708rad)
  sketch-geometry (4):
    g0: LineSegment StartX=7 StartY=0 StartZ=0 EndX=10 EndY=0 EndZ=0
    g1: LineSegment StartX=11 StartY=-1 StartZ=0 EndX=11 EndY=-2 EndZ=0
    g2: ArcOfCircle CenterX=10 CenterY=-1 CenterZ=0 NormalX=0 NormalY=0 NormalZ=1 AngleXU=0 Radius=1 StartAngle=0 EndAngle=1.5708
    g3: GeomPoint [constr] X=11 Y=0 Z=0
  constraints (11):
    c: Horizontal(g0)
    c: Vertical(g1)
    c: PointOnObject(g3,g0)
    c: PointOnObject(g3,g1)
    c: Tangent(g0,g2) = 1.5708
    c: Tangent(g1,g2) = 1.5708
    c: PointOnObject(g0,g-3)
    c: PointOnObject(g0,g-1)
    c: Radius(g2) = 1
    c: DistanceX(g0,g1) = 4
    c: DistanceY(g1,g0) = 2
FEATURE [PartDesign::AdditivePipe] AdditivePipe
  AuxilleryCurvelinear = true
  AuxillerySpineTangent = false
  BaseFeature = -> Pad108
  Binormal = (0,0,0)
  Mode = 0
  Placement = pos=(0,0,0) rot=(1,1,1;2.0944rad)
  Profile = -> Sketch222
  Spine = -> Sketch223
  SpineTangent = false
  Suppressed = false
  Transformation = 0
  Transition = 0
FEATURE [PartDesign::Mirrored] Mirrored008
  BaseFeature = -> AdditivePipe
  MirrorPlane = -> YZ_Plane276
  Placement = pos=(0,0,0) rot=(1,1,1;2.0944rad)
  Refine = true
  Suppressed = false
  TransformMode = 1
FEATURE [PartDesign::Body] Body080  label="capteur_reed"
  AllowCompound = false
  Group = -> [Sketch221,Pad108,Sketch222,Sketch223,AdditivePipe,Mirrored008]
  Origin = -> Origin279
  Placement = pos=(38,7.5,-4) rot=(0,0,1;0rad)
  Tip = -> Mirrored008
FEATURE [App::Link] Link001  label="capteur_reed001"
  LinkPlacement = pos=(124,0,0) rot=(0,0,1;0rad)
  LinkTransform = true
  LinkedObject = -> Body080
  Placement = pos=(124,0,0) rot=(0,0,1;0rad)
FEATURE [Sketcher::SketchObject] Sketch224
  ArcFitTolerance = 1e-06
  AttachmentSupport = -> [Pocket084]
  ExternalGeometry = -> [Pocket084]
  FullyConstrained = true
  MakeInternals = false
  MapMode = 5
  Placement = pos=(-1.2e-15,6.8e-15,-4.1) rot=(0,0,-1;1.5708rad)
  sketch-geometry (2):
    g0: Circle CenterX=0 CenterY=35 CenterZ=0 NormalX=0 NormalY=0 NormalZ=1 AngleXU=0 Radius=2.1
    g1: Circle CenterX=1.06e-14 CenterY=10 CenterZ=0 NormalX=0 NormalY=0 NormalZ=1 AngleXU=0 Radius=2.1
  constraints (4):
    c: Diameter(g0) = 4.2
    c: Coincident(g0,g-3)
    c: Coincident(g1,g-4)
    c: Diameter(g1) = 4.2
FEATURE [PartDesign::Pocket] Pocket090  label="insert"
  BaseFeature = -> Pocket084
  Direction = (0,1.4e-15,-1)
  Length = 3
  Length2 = 5
  Placement = pos=(0,0,0) rot=(1,1,1;2.0944rad)
  Profile = -> Sketch224
  ReferenceAxis = -> Sketch224 [N_Axis]
  Suppressed = false
  Type = 0
FEATURE [Sketcher::SketchObject] Sketch227
  ArcFitTolerance = 1e-06
  AttachmentSupport = -> [YZ_Plane277]
  FullyConstrained = true
  MakeInternals = false
  MapMode = 5
  Placement = pos=(0,0,0) rot=(0.57735,0.57735,0.57735;2.0944rad)
  sketch-geometry (1):
    g0: Circle CenterX=0 CenterY=0 CenterZ=0 NormalX=0 NormalY=0 NormalZ=1 AngleXU=0 Radius=1.05
  constraints (2):
    c: Diameter(g0) = 2.1
    c: Coincident(g0,g-1)
FEATURE [Sketcher::SketchObject] Sketch228
  ArcFitTolerance = 1e-06
  AttachmentSupport = -> [XY_Plane277]
  FullyConstrained = true
  MakeInternals = false
  MapMode = 5
  sketch-geometry (4):
    g0: LineSegment StartX=-4 StartY=1 StartZ=0 EndX=-4 EndY=-1.5 EndZ=0
    g1: LineSegment StartX=-4 StartY=-1.5 StartZ=0 EndX=4 EndY=-1.5 EndZ=0
    g2: LineSegment StartX=4 StartY=-1.5 StartZ=0 EndX=4 EndY=1 EndZ=0
    g3: LineSegment StartX=4 StartY=1 StartZ=0 EndX=-4 EndY=1 EndZ=0
  constraints (11):
    c: Coincident(g0,g1)
    c: Coincident(g1,g2)
    c: Coincident(g2,g3)
    c: Coincident(g3,g0)
    c: Vertical(g0)
    c: Vertical(g2)
    c: Horizontal(g1)
    c: Symmetric(g2,g0,g-2)
    c: DistanceY(g-1,g0) = 1
    c: DistanceX(g3,g3) = 8
    c: DistanceY(g1,g-1) = 1.5
FEATURE [PartDesign::Pad] Pad110
  Direction = (0,0,1)
  Length = 2
  Length2 = 6
  Profile = -> Sketch228
  ReferenceAxis = -> Sketch228 [N_Axis]
  Suppressed = false
  Type = 4
FEATURE [PartDesign::Pocket] Pocket092
  BaseFeature = -> Pad110
  Direction = (-1,0,0)
  Length = 5
  Length2 = 5
  Midplane = true
  Profile = -> Sketch227
  ReferenceAxis = -> Sketch227 [N_Axis]
  Suppressed = false
  Type = 1
FEATURE [Sketcher::SketchObject] Sketch229
  ArcFitTolerance = 1e-06
  AttachmentSupport = -> [Pocket092]
  ExternalGeometry = -> [Pocket092]
  FullyConstrained = true
  MakeInternals = false
  MapMode = 5
  Placement = pos=(0,0,-6) rot=(1,0,0;3.14159rad)
  expr: Constraints[14] = 3.5 / 2
  sketch-geometry (9):
    g0: ArcOfCircle CenterX=-5 CenterY=7.5 CenterZ=0 NormalX=0 NormalY=0 NormalZ=1 AngleXU=0 Radius=1.75 StartAngle=1.5708 EndAngle=4.71239
    g1: LineSegment StartX=-5 StartY=9.25 StartZ=0 EndX=0 EndY=9.25 EndZ=0
    g2: LineSegment StartX=-5 StartY=5.75 StartZ=0 EndX=0 EndY=5.75 EndZ=0
    g3: LineSegment StartX=0 StartY=1.5 StartZ=0 EndX=-4 EndY=1.5 EndZ=0
    g4: LineSegment StartX=0 StartY=10.5 StartZ=0 EndX=-5 EndY=10.5 EndZ=0
    g5: LineSegment StartX=0 StartY=10.5 StartZ=0 EndX=0 EndY=9.25 EndZ=0
    g6: LineSegment StartX=0 StartY=5.75 StartZ=0 EndX=0 EndY=1.5 EndZ=0
    g7: ArcOfCircle CenterX=-5 CenterY=7.5 CenterZ=0 NormalX=0 NormalY=0 NormalZ=1 AngleXU=0 Radius=3 StartAngle=1.5708 EndAngle=3.8225
    g8: LineSegment StartX=-4 StartY=1.5 StartZ=0 EndX=-7.331 EndY=5.6115 EndZ=0
  constraints (23):
    c: Tangent(g0,g1) = 1.5708
    c: Tangent(g0,g2) = -1.5708
    c: Horizontal(g2)
    c: PointOnObject(g1,g-2)
    c: PointOnObject(g2,g-2)
    c: Horizontal(g1)
    c: Symmetric(g-3,g-3,g3)
    c: Coincident(g3,g-3)
    c: PointOnObject(g4,g-2)
    c: Horizontal(g4)
    c: Coincident(g5,g4)
    c: Coincident(g5,g1)
    c: Coincident(g6,g2)
    c: Coincident(g6,g3)
    c: Radius(g0) = 1.75
    c: Vertical(g1,g4)
    c: DistanceX(g0,g2) = 5
    c: DistanceY(g-1,g0) = 7.5
    c: Coincident(g7,g0)
    c: Coincident(g7,g4)
    c: Coincident(g8,g3)
    c: Tangent(g8,g7) = 1.5708
    c: Radius(g7) = 3
FEATURE [PartDesign::Pad] Pad111
  BaseFeature = -> Pocket092
  Direction = (0,0,-1)
  Length = 4
  Length2 = 10
  Profile = -> Sketch229
  ReferenceAxis = -> Sketch229 [N_Axis]
  Reversed = true
  Suppressed = false
  Type = 0
FEATURE [PartDesign::Mirrored] Mirrored009
  BaseFeature = -> Pad111
  MirrorPlane = -> Sketch229 [V_Axis]
  Originals = -> [Pad111]
  Refine = true
  Suppressed = false
  TransformMode = 0
FEATURE [PartDesign::Fillet] Fillet001
  Base = -> Mirrored009 [Edge16,Edge19]
  BaseFeature = -> Mirrored009
  Radius = 0.4
  SupportTransform = false
  Suppressed = false
  UseAllEdges = false
FEATURE [PartDesign::Chamfer] Chamfer006
  Angle = 45
  Base = -> Fillet001 [Edge26]
  BaseFeature = -> Fillet001
  ChamferType = 0
  FlipDirection = false
  Size = 2
  Size2 = 2
  SupportTransform = false
  Suppressed = false
  UseAllEdges = false
FEATURE [PartDesign::Body] Body081  label="support_capteur_reed"
  AllowCompound = false
  Group = -> [Sketch227,Sketch228,Pad110,Pocket092,Sketch229,Pad111,Mirrored009,Fillet001,Chamfer006]
  Origin = -> Origin280
  Placement = pos=(162,7.5,-13) rot=(0,0,1;0rad)
  Tip = -> Chamfer006
FEATURE [Sketcher::SketchObject] Sketch230
  ArcFitTolerance = 1e-06
  AttachmentSupport = -> [LinearPattern]
  ExternalGeometry = -> [LinearPattern]
  FullyConstrained = true
  MakeInternals = false
  MapMode = 5
  Placement = pos=(0,0,0) rot=(1,0,0;3.14159rad)
  sketch-geometry (1):
    g0: Circle CenterX=-12.5 CenterY=-108.5 CenterZ=0 NormalX=0 NormalY=0 NormalZ=1 AngleXU=0 Radius=1.7
  constraints (2):
    c: Coincident(g0,g-3)
    c: Equal(g0,g-3)
FEATURE [PartDesign::Pad] Pad112
  BaseFeature = -> LinearPattern
  Direction = (0,0,-1)
  Length = 5
  Length2 = 10
  Profile = -> Sketch230
  ReferenceAxis = -> Sketch230 [N_Axis]
  Reversed = true
  Suppressed = false
  Type = 0
FEATURE [Sketcher::SketchObject] Sketch233
  ArcFitTolerance = 1e-06
  AttachmentSupport = -> [Pad112]
  FullyConstrained = true
  MakeInternals = false
  MapMode = 5
  Placement = pos=(0,0,0) rot=(1,0,0;3.14159rad)
  sketch-geometry (11):
    g0: LineSegment StartX=-16.5 StartY=-107.5 StartZ=0 EndX=-16.5 EndY=-113.5 EndZ=0
    g1: LineSegment StartX=-14.5 StartY=-115.5 StartZ=0 EndX=-10.5 EndY=-115.5 EndZ=0
    g2: LineSegment StartX=-8.5 StartY=-113.5 StartZ=0 EndX=-8.5 EndY=-107.5 EndZ=0
    g3: LineSegment StartX=-10.5 StartY=-105.5 StartZ=0 EndX=-14.5 EndY=-105.5 EndZ=0
    g4: ArcOfCircle CenterX=-14.5 CenterY=-107.5 CenterZ=0 NormalX=0 NormalY=0 NormalZ=1 AngleXU=0 Radius=2 StartAngle=1.5708 EndAngle=3.14159
    g5: ArcOfCircle CenterX=-14.5 CenterY=-113.5 CenterZ=0 NormalX=0 NormalY=0 NormalZ=1 AngleXU=0 Radius=2 StartAngle=3.14159 EndAngle=4.71239
    g6: ArcOfCircle CenterX=-10.5 CenterY=-113.5 CenterZ=0 NormalX=0 NormalY=0 NormalZ=1 AngleXU=0 Radius=2 StartAngle=4.71239 EndAngle=6.28319
    g7: ArcOfCircle CenterX=-10.5 CenterY=-107.5 CenterZ=0 NormalX=0 NormalY=0 NormalZ=1 AngleXU=0 Radius=2 StartAngle=-1.8e-15 EndAngle=1.5708
    g8: GeomPoint [constr] X=-16.5 Y=-105.5 Z=0
    g9: GeomPoint [constr] X=-8.5 Y=-115.5 Z=0
    g10: GeomPoint X=-12.5 Y=-110.5 Z=0
  constraints (25):
    c: Tangent(g0,g4) = -1.5708
    c: Tangent(g0,g5) = -1.5708
    c: Tangent(g1,g5) = -1.5708
    c: Tangent(g1,g6) = -1.5708
    c: Tangent(g2,g6) = -1.5708
    c: Tangent(g2,g7) = -1.5708
    c: Tangent(g3,g7) = -1.5708
    c: Tangent(g3,g4) = -1.5708
    c: Vertical(g0)
    c: Vertical(g2)
    c: Horizontal(g1)
    c: Horizontal(g3)
    c: Equal(g4,g5)
    c: Equal(g5,g6)
    c: Equal(g6,g7)
    c: PointOnObject(g8,g0)
    c: PointOnObject(g8,g3)
    c: PointOnObject(g9,g1)
    c: PointOnObject(g9,g2)
    c: Symmetric(g7,g5,g10)
    c: DistanceX(g10,g-1) = 12.5
    c: DistanceY(g10,g-1) = 110.5
    c: Radius(g4) = 2
    c: DistanceY(g1,g3) = 10
    c: DistanceX(g0,g2) = 8
FEATURE [PartDesign::Pad] Pad113
  BaseFeature = -> Pad112
  Direction = (0,0,-1)
  Length = 1
  Length2 = 10
  Profile = -> Sketch233
  ReferenceAxis = -> Sketch233 [N_Axis]
  Suppressed = false
  Type = 0
FEATURE [Sketcher::SketchObject] Sketch231
  ArcFitTolerance = 1e-06
  AttachmentSupport = -> [Pad113]
  FullyConstrained = true
  MakeInternals = false
  MapMode = 5
  Placement = pos=(0,0,-1) rot=(1,0,0;3.14159rad)
  sketch-geometry (1):
    g0: Circle CenterX=-12.5 CenterY=-110.5 CenterZ=0 NormalX=0 NormalY=0 NormalZ=1 AngleXU=0 Radius=1.85
  constraints (3):
    c: Diameter(g0) = 3.7
    c: DistanceY(g0,g-1) = 110.5
    c: DistanceX(g0,g-1) = 12.5
FEATURE [Sketcher::SketchObject] Sketch232
  ArcFitTolerance = 1e-06
  AttachmentSupport = -> [Pad113]
  FullyConstrained = true
  MakeInternals = false
  MapMode = 5
  Placement = pos=(0,0,-1) rot=(1,0,0;3.14159rad)
  sketch-geometry (1):
    g0: Circle CenterX=-12.5 CenterY=-110.5 CenterZ=0 NormalX=0 NormalY=0 NormalZ=1 AngleXU=0 Radius=2.1
  constraints (2):
    c: Diameter(g0) = 4.2
    c: Coincident(g0,g-3)
FEATURE [PartDesign::Pocket] Pocket094
  BaseFeature = -> Pad113
  Direction = (0,0,1)
  Length = 3
  Length2 = 5
  Profile = -> Sketch232
  ReferenceAxis = -> Sketch232 [N_Axis]
  Suppressed = false
  Type = 0
FEATURE [PartDesign::Pocket] Pocket093
  BaseFeature = -> Pocket094
  Direction = (0,0,1)
  Length = 6
  Length2 = 5
  Profile = -> Sketch231
  ReferenceAxis = -> Sketch231 [N_Axis]
  Suppressed = false
  Type = 0
FEATURE [PartDesign::Body] Body073  label="crémaillère"
  AllowCompound = false
  BaseFeature = -> InvoluteRack
  Group = -> [BaseFeature002,Sketch192,Pocket074,LinearPattern,Sketch193,Sketch230,Pad112,Sketch231,Sketch233,Pad113,Pocket094,Pocket093,Sketch232]
  Origin = -> Origin272
  Placement = pos=(51.5,-12.5,-14) rot=(0,0,1;4.71239rad)
  Tip = -> LinearPattern
FEATURE [Sketcher::SketchObject] Sketch240
  ArcFitTolerance = 1e-06
  AttachmentSupport = -> [XY_Plane279]
  FullyConstrained = true
  MakeInternals = false
  MapMode = 5
  sketch-geometry (5):
    g0: LineSegment StartX=-6 StartY=6 StartZ=0 EndX=-6 EndY=-6 EndZ=0
    g1: LineSegment StartX=-6 StartY=-6 StartZ=0 EndX=6 EndY=-6 EndZ=0
    g2: LineSegment StartX=6 StartY=-6 StartZ=0 EndX=6 EndY=6 EndZ=0
    g3: LineSegment StartX=6 StartY=6 StartZ=0 EndX=-6 EndY=6 EndZ=0
    g4: Circle CenterX=0 CenterY=0 CenterZ=0 NormalX=0 NormalY=0 NormalZ=1 AngleXU=0 Radius=1.75
  constraints (13):
    c: Coincident(g0,g1)
    c: Coincident(g1,g2)
    c: Coincident(g2,g3)
    c: Coincident(g3,g0)
    c: Vertical(g0)
    c: Vertical(g2)
    c: Horizontal(g1)
    c: Horizontal(g3)
    c: Diameter(g4) = 3.5
    c: Coincident(g4,g-1)
    c: Symmetric(g2,g0,g4)
    c: Equal(g3,g0)
    c: DistanceX(g3,g3) = 12
FEATURE [PartDesign::Pad] Pad116
  Direction = (0,0,1)
  Length = 9
  Length2 = 10
  Profile = -> Sketch240
  ReferenceAxis = -> Sketch240 [N_Axis]
  Suppressed = false
  Type = 0
FEATURE [PartDesign::Body] Body083  label="cremaillere_spacer"
  AllowCompound = false
  Group = -> [Sketch240,Pad116]
  Origin = -> Origin282
  Placement = pos=(60,0,-9) rot=(0,0,1;0rad)
  Tip = -> Pad116
FEATURE [App::Link] Link002  label="cremaillere_spacer001"
  LinkPlacement = pos=(125,0,0) rot=(0,0,1;0rad)
  LinkTransform = true
  LinkedObject = -> Body083
  Placement = pos=(125,0,0) rot=(0,0,1;0rad)
FEATURE [Sketcher::SketchObject] Sketch241
  ArcFitTolerance = 1e-06
  AttachmentSupport = -> [YZ_Plane282]
  FullyConstrained = true
  MakeInternals = false
  MapMode = 5
  Placement = pos=(0,0,0) rot=(0.57735,0.57735,0.57735;2.0944rad)
  expr: Constraints[48] = 135
  sketch-geometry (23):
    g0: LineSegment StartX=-10 StartY=5.25 StartZ=0 EndX=-10 EndY=-4.25 EndZ=0
    g1: LineSegment StartX=-9.5 StartY=-4.75 StartZ=0 EndX=-6.15 EndY=-4.75 EndZ=0
    g2: LineSegment StartX=10 StartY=-4.25 StartZ=0 EndX=10 EndY=4.25 EndZ=0
    g3: LineSegment StartX=9.5 StartY=4.75 StartZ=0 EndX=-1.8e-15 EndY=4.75 EndZ=0
    g4: ArcOfCircle CenterX=-9.5 CenterY=5.25 CenterZ=0 NormalX=0 NormalY=0 NormalZ=1 AngleXU=0 Radius=0.5 StartAngle=1.5708 EndAngle=3.14159
    g5: ArcOfCircle CenterX=-9.5 CenterY=-4.25 CenterZ=0 NormalX=0 NormalY=0 NormalZ=1 AngleXU=0 Radius=0.5 StartAngle=3.14159 EndAngle=4.71239
    g6: ArcOfCircle CenterX=9.5 CenterY=-4.25 CenterZ=0 NormalX=0 NormalY=0 NormalZ=1 AngleXU=0 Radius=0.5 StartAngle=4.71239 EndAngle=6.28319
    g7: ArcOfCircle CenterX=9.5 CenterY=4.25 CenterZ=0 NormalX=0 NormalY=0 NormalZ=1 AngleXU=0 Radius=0.5 StartAngle=0 EndAngle=1.5708
    g8: GeomPoint [constr] X=-10 Y=4.75 Z=0
    g9: GeomPoint [constr] X=10 Y=-4.75 Z=0
    g10: Circle CenterX=-4.65 CenterY=-2.1 CenterZ=0 NormalX=0 NormalY=0 NormalZ=1 AngleXU=0 Radius=1.15
    g11: Circle CenterX=4.65 CenterY=-2.1 CenterZ=0 NormalX=0 NormalY=0 NormalZ=1 AngleXU=0 Radius=1.15
    g12: LineSegment StartX=-1.2e-15 StartY=4.75 StartZ=0 EndX=-1 EndY=5.75 EndZ=0
    g13: LineSegment StartX=-1 StartY=5.75 StartZ=0 EndX=-9.5 EndY=5.75 EndZ=0
    g14: LineSegment StartX=-6.15 StartY=-4.75 StartZ=0 EndX=-5.9 EndY=-4.95 EndZ=0
    g15: LineSegment StartX=-5.9 StartY=-4.95 StartZ=0 EndX=-3.4 EndY=-4.95 EndZ=0
    g16: LineSegment StartX=-3.4 StartY=-4.95 StartZ=0 EndX=-3.15 EndY=-4.75 EndZ=0
    g17: LineSegment StartX=3.15 StartY=-4.75 StartZ=0 EndX=3.4 EndY=-4.95 EndZ=0
    g18: LineSegment StartX=3.4 StartY=-4.95 StartZ=0 EndX=5.9 EndY=-4.95 EndZ=0
    g19: LineSegment StartX=5.9 StartY=-4.95 StartZ=0 EndX=6.15 EndY=-4.75 EndZ=0
    g20: LineSegment StartX=-3.15 StartY=-4.75 StartZ=0 EndX=3.15 EndY=-4.75 EndZ=0
    g21: LineSegment StartX=6.15 StartY=-4.75 StartZ=0 EndX=9.5 EndY=-4.75 EndZ=0
    g22: GeomPoint X=-4.65 Y=-4.95 Z=0
  constraints (58):
    c: Tangent(g0,g4) = -1.5708
    c: Tangent(g0,g5) = -1.5708
    c: Tangent(g1,g5) = -1.5708
    c: Tangent(g2,g6) = -1.5708
    c: Tangent(g2,g7) = -1.5708
    c: Tangent(g3,g7) = -1.5708
    c: Vertical(g0)
    c: Vertical(g2)
    c: Horizontal(g1)
    c: Horizontal(g3)
    c: Equal(g5,g6)
    c: Equal(g6,g7)
    c: PointOnObject(g8,g0)
    c: PointOnObject(g8,g3)
    c: PointOnObject(g9,g21)
    c: PointOnObject(g9,g2)
    c: Coincident(g13,g12)
    c: Horizontal(g13)
    c: Coincident(g15,g14)
    c: Horizontal(g15)
    c: Coincident(g16,g15)
    c: PointOnObject(g16,g20)
    c: Coincident(g19,g18)
    c: Coincident(g17,g18)
    c: Horizontal(g18)
    c: Symmetric(g16,g17,g-2)
    c: Equal(g16,g17)
    c: Equal(g18,g15)
    c: Equal(g14,g16)
    c: Equal(g17,g19)
    c: Symmetric(g19,g14,g-2)
    c: PointOnObject(g20,g16)
    c: Coincident(g1,g14)
    c: Symmetric(g11,g10,g-2)
    c: Coincident(g3,g12)
    c: Coincident(g21,g19)
    c: Coincident(g17,g20)
    c: Horizontal(g1,g16)
    c: Horizontal(g21)
    c: DistanceY(g9,g8) = 9.5
    c: Tangent(g4,g13) = -1.5708
    c: Diameter(g10) = 2.3
    c: Equal(g10,g11)
    c: DistanceX(g0,g2) = 20
    c: Equal(g7,g4)
    c: Tangent(g21,g6) = -1.5708
    c: Radius(g4) = 0.5
    c: DistanceY(g1,g4) = 10.5
    c: Angle(g3,g12) = 2.35619
    c: DistanceX(g8,g3) = 10
    c: DistanceY(g17,g17) = 0.2
    c: Distance(g10,g11) = 7
    c: Distance(g11,g18) = 1.7
    c: Symmetric(g7,g5,g-1)
    c: DistanceX(g15,g15) = 2.5
    c: DistanceX(g1,g16) = 3
    c: Symmetric(g15,g15,g22)
    c: Vertical(g22,g10)
FEATURE [PartDesign::Pad] Pad117
  Direction = (1,0,0)
  Length = 6.5
  Length2 = 10
  Midplane = true
  Placement = pos=(0,0,0) rot=(1,1,1;2.0944rad)
  Profile = -> Sketch241
  ReferenceAxis = -> Sketch241 [N_Axis]
  Suppressed = false
  Type = 0
FEATURE [PartDesign::Body] Body084  label="Corps"
  AllowCompound = false
  Group = -> [Sketch241,Pad117]
  Origin = -> Origin285
  Tip = -> Pad117
FEATURE [Sketcher::SketchObject] Sketch242
  ArcFitTolerance = 1e-06
  AttachmentSupport = -> [YZ_Plane283]
  FullyConstrained = true
  MakeInternals = false
  MapMode = 5
  Placement = pos=(0,0,0) rot=(0.57735,0.57735,0.57735;2.0944rad)
  sketch-geometry (8):
    g0: LineSegment StartX=-1.65 StartY=0 StartZ=0 EndX=-1.65 EndY=-3.5 EndZ=0
    g1: LineSegment StartX=-1.15 StartY=-4 StartZ=0 EndX=1.15 EndY=-4 EndZ=0
    g2: LineSegment StartX=1.65 StartY=-3.5 StartZ=0 EndX=1.65 EndY=0 EndZ=0
    g3: LineSegment StartX=1.65 StartY=0 StartZ=0 EndX=-1.65 EndY=0 EndZ=0
    g4: ArcOfCircle CenterX=-1.15 CenterY=-3.5 CenterZ=0 NormalX=0 NormalY=0 NormalZ=1 AngleXU=0 Radius=0.5 StartAngle=3.14159 EndAngle=4.71239
    g5: ArcOfCircle CenterX=1.15 CenterY=-3.5 CenterZ=0 NormalX=0 NormalY=0 NormalZ=1 AngleXU=0 Radius=0.5 StartAngle=4.71239 EndAngle=6.28319
    g6: GeomPoint [constr] X=1.65 Y=-4 Z=0
    g7: Circle CenterX=0 CenterY=-2.5 CenterZ=0 NormalX=0 NormalY=0 NormalZ=1 AngleXU=0 Radius=0.75
  constraints (20):
    c: Tangent(g0,g4) = -1.5708
    c: Tangent(g1,g4) = -1.5708
    c: Tangent(g1,g5) = -1.5708
    c: Tangent(g2,g5) = -1.5708
    c: Vertical(g0)
    c: Vertical(g2)
    c: Horizontal(g1)
    c: Horizontal(g3)
    c: Equal(g4,g5)
    c: PointOnObject(g6,g1)
    c: PointOnObject(g6,g2)
    c: PointOnObject(g7,g-2)
    c: Coincident(g0,g3)
    c: Coincident(g2,g3)
    c: Symmetric(g0,g2,g-1)
    c: Diameter(g7) = 1.5
    c: DistanceX(g3,g3) = 3.3
    c: Radius(g5) = 0.5
    c: DistanceY(g1,g-1) = 4
    c: DistanceY(g7,g-1) = 2.5
FEATURE [PartDesign::Pad] Pad118
  Direction = (1,0,0)
  Length = 0.4
  Length2 = 10
  Midplane = true
  Placement = pos=(0,0,0) rot=(1,1,1;2.0944rad)
  Profile = -> Sketch242
  ReferenceAxis = -> Sketch242 [N_Axis]
  Suppressed = false
  Type = 0
FEATURE [PartDesign::Body] Body085  label="contact"
  AllowCompound = false
  Group = -> [Sketch242,Pad118]
  Origin = -> Origin286
  Placement = pos=(0,8.5,-4.7) rot=(0,0,1;4.71239rad)
  Tip = -> Pad118
FEATURE [App::LinkElement] Link004_i0
  LinkPlacement = pos=(0,-7.5,0) rot=(0,0,1;0rad)
  LinkTransform = true
  LinkedObject = -> Body085
  Placement = pos=(0,-7.5,0) rot=(0,0,1;0rad)
  _LinkOwner = 787
FEATURE [App::LinkElement] Link004_i1
  LinkPlacement = pos=(0,-16.5,0) rot=(0,0,1;0rad)
  LinkTransform = true
  LinkedObject = -> Body085
  Placement = pos=(0,-16.5,0) rot=(0,0,1;0rad)
  _LinkOwner = 787
  expr: .LinkPlacement.Base.y = -7.5 - 9
FEATURE [App::Link] Link004  label="contacts"
  ElementCount = 2
  ElementList = -> [Link004_i0,Link004_i1]
  LinkTransform = true
  LinkedObject = -> Body085
FEATURE [Sketcher::SketchObject] Sketch243
  ArcFitTolerance = 1e-06
  AttachmentSupport = -> [YZ_Plane284]
  FullyConstrained = true
  MakeInternals = false
  MapMode = 5
  Placement = pos=(0,0,0) rot=(0.57735,0.57735,0.57735;2.0944rad)
  sketch-geometry (6):
    g0: LineSegment StartX=-0.1 StartY=0 StartZ=0 EndX=0.1 EndY=0 EndZ=0
    g1: LineSegment StartX=0.1 StartY=0 StartZ=0 EndX=0.1 EndY=1.84653 EndZ=0
    g2: LineSegment StartX=0.1 StartY=1.84653 StartZ=0 EndX=15.9518 EndY=6.094 EndZ=0
    g3: LineSegment StartX=15.9518 StartY=6.094 StartZ=0 EndX=15.9 EndY=6.28719 EndZ=0
    g4: LineSegment StartX=15.9 StartY=6.28719 StartZ=0 EndX=-0.1 EndY=2 EndZ=0
    g5: LineSegment StartX=-0.1 StartY=2 StartZ=0 EndX=-0.1 EndY=0 EndZ=0
  constraints (17):
    c: PointOnObject(g0,g-1)
    c: Coincident(g0,g1)
    c: Vertical(g1)
    c: Coincident(g1,g2)
    c: Coincident(g2,g3)
    c: Coincident(g3,g4)
    c: Coincident(g4,g5)
    c: Coincident(g5,g0)
    c: Vertical(g5)
    c: Symmetric(g0,g0,g-1)
    c: Perpendicular(g2,g3)
    c: Equal(g3,g0)
    c: Parallel(g2,g4)
    c: DistanceX(g0,g0) = 0.2
    c: Angle(g-1,g2) = 0.261799
    c: DistanceX(g4,g3) = 16
    c: DistanceY(g-1,g4) = 2
FEATURE [PartDesign::Pad] Pad119
  Direction = (1,0,0)
  Length = 4
  Length2 = 10
  Midplane = true
  Placement = pos=(0,0,0) rot=(1,1,1;2.0944rad)
  Profile = -> Sketch243
  ReferenceAxis = -> Sketch243 [N_Axis]
  Suppressed = false
  Type = 0
FEATURE [PartDesign::Body] Body086  label="Corps002"
  AllowCompound = false
  Group = -> [Sketch243,Pad119]
  Origin = -> Origin287
  Placement = pos=(0,-8,5) rot=(1,0,0;6.02139rad)
  Tip = -> Pad119
FEATURE [App::Part] Part002008  label="micro_switch"
  Group = -> [Body084,Body085,Body086,Link004]
  Origin = -> Origin284
  Placement = pos=(12,20,0) rot=(0.57735,0.57735,0.57735;2.0944rad)
FEATURE [App::Link] Link005  label="micro_switch001"
  LinkPlacement = pos=(3.8147e-06,6.49909e-08,-5.96976e-07) rot=(0.57735,-0.57735,-0.57735;2.0944rad)
  LinkedObject = -> Part002008
  Placement = pos=(3.8147e-06,6.49909e-08,-5.96976e-07) rot=(0.57735,-0.57735,-0.57735;2.0944rad)
FEATURE [Sketcher::SketchObject] Sketch244
  ArcFitTolerance = 1e-06
  AttachmentSupport = -> [XY_Plane285]
  FullyConstrained = true
  MakeInternals = false
  MapMode = 5
  sketch-geometry (10):
    g0: LineSegment StartX=-11 StartY=3.7 StartZ=0 EndX=-11 EndY=-5 EndZ=0
    g1: LineSegment StartX=-10 StartY=-6 StartZ=0 EndX=10 EndY=-6 EndZ=0
    g2: LineSegment StartX=11 StartY=-5 StartZ=0 EndX=11 EndY=3.7 EndZ=0
    g3: LineSegment StartX=10 StartY=4.7 StartZ=0 EndX=-10 EndY=4.7 EndZ=0
    g4: ArcOfCircle CenterX=-10 CenterY=3.7 CenterZ=0 NormalX=0 NormalY=0 NormalZ=1 AngleXU=0 Radius=1 StartAngle=1.5708 EndAngle=3.14159
    g5: ArcOfCircle CenterX=-10 CenterY=-5 CenterZ=0 NormalX=0 NormalY=0 NormalZ=1 AngleXU=0 Radius=1 StartAngle=3.14159 EndAngle=4.71239
    g6: ArcOfCircle CenterX=10 CenterY=-5 CenterZ=0 NormalX=0 NormalY=0 NormalZ=1 AngleXU=0 Radius=1 StartAngle=4.71239 EndAngle=6.28319
    g7: ArcOfCircle CenterX=10 CenterY=3.7 CenterZ=0 NormalX=0 NormalY=0 NormalZ=1 AngleXU=0 Radius=1 StartAngle=0 EndAngle=1.5708
    g8: GeomPoint [constr] X=-11 Y=4.7 Z=0
    g9: GeomPoint [constr] X=11 Y=-6 Z=0
  constraints (23):
    c: Tangent(g0,g4) = -1.5708
    c: Tangent(g0,g5) = -1.5708
    c: Tangent(g1,g5) = -1.5708
    c: Tangent(g1,g6) = -1.5708
    c: Tangent(g2,g6) = -1.5708
    c: Tangent(g2,g7) = -1.5708
    c: Tangent(g3,g7) = -1.5708
    c: Tangent(g3,g4) = -1.5708
    c: Vertical(g0)
    c: Vertical(g2)
    c: Horizontal(g3)
    c: Equal(g4,g5)
    c: Equal(g5,g6)
    c: Equal(g6,g7)
    c: PointOnObject(g8,g0)
    c: PointOnObject(g8,g3)
    c: PointOnObject(g9,g1)
    c: PointOnObject(g9,g2)
    c: Radius(g4) = 1
    c: DistanceX(g0,g2) = 22
    c: DistanceY(g1,g-1) = 6
    c: Symmetric(g1,g1,g-2)
    c: DistanceY(g-1,g2) = 3.7
FEATURE [PartDesign::Pad] Pad120
  Direction = (0,0,1)
  Length = 10
  Length2 = 10
  Midplane = true
  Profile = -> Sketch244
  ReferenceAxis = -> Sketch244 [N_Axis]
  Suppressed = false
  Type = 0
FEATURE [Sketcher::SketchObject] Sketch245
  ArcFitTolerance = 1e-06
  AttachmentSupport = -> [XY_Plane285]
  FullyConstrained = true
  MakeInternals = false
  MapMode = 5
  sketch-geometry (17):
    g0: LineSegment StartX=-10.05 StartY=10 StartZ=0 EndX=-10.05 EndY=-5 EndZ=0
    g1: LineSegment StartX=-10.05 StartY=-5 StartZ=0 EndX=-9.5 EndY=-5 EndZ=0
    g2: LineSegment StartX=10.05 StartY=-5 StartZ=0 EndX=10.05 EndY=10 EndZ=0
    g3: LineSegment StartX=10.05 StartY=10 StartZ=0 EndX=-10.05 EndY=10 EndZ=0
    g4: LineSegment StartX=-9.5 StartY=-5 StartZ=0 EndX=-9.5 EndY=-12 EndZ=0
    g5: LineSegment StartX=-9.5 StartY=-12 StartZ=0 EndX=-7.5 EndY=-12 EndZ=0
    g6: LineSegment StartX=-7.5 StartY=-12 StartZ=0 EndX=-7.5 EndY=-5 EndZ=0
    g7: LineSegment StartX=-2 StartY=-5 StartZ=0 EndX=-2 EndY=-12 EndZ=0
    g8: LineSegment StartX=-2 StartY=-12 StartZ=0 EndX=0 EndY=-12 EndZ=0
    g9: LineSegment StartX=0 StartY=-12 StartZ=0 EndX=0 EndY=-5 EndZ=0
    g10: LineSegment StartX=7 StartY=-5 StartZ=0 EndX=7 EndY=-12 EndZ=0
    g11: LineSegment StartX=7 StartY=-12 StartZ=0 EndX=9 EndY=-12 EndZ=0
    g12: LineSegment StartX=9 StartY=-12 StartZ=0 EndX=9 EndY=-5 EndZ=0
    g13: LineSegment StartX=9 StartY=-5 StartZ=0 EndX=10.05 EndY=-5 EndZ=0
    g14: LineSegment StartX=0 StartY=-5 StartZ=0 EndX=7 EndY=-5 EndZ=0
    g15: LineSegment StartX=-7.5 StartY=-5 StartZ=0 EndX=-2 EndY=-5 EndZ=0
    g16: LineSegment [constr] StartX=-9.5 StartY=-5 StartZ=0 EndX=9 EndY=-5 EndZ=0
  constraints (49):
    c: Coincident(g0,g1)
    c: Coincident(g13,g2)
    c: Coincident(g2,g3)
    c: Coincident(g3,g0)
    c: Vertical(g0)
    c: Vertical(g2)
    c: Horizontal(g1)
    c: Coincident(g4,g5)
    c: Coincident(g5,g6)
    c: Vertical(g4)
    c: Vertical(g6)
    c: Horizontal(g5)
    c: Coincident(g7,g8)
    c: Coincident(g8,g9)
    c: Vertical(g7)
    c: Vertical(g9)
    c: Horizontal(g8)
    c: Coincident(g10,g11)
    c: Coincident(g11,g12)
    c: Vertical(g10)
    c: Vertical(g12)
    c: Horizontal(g11)
    c: Coincident(g1,g4)
    c: Coincident(g14,g10)
    c: Coincident(g9,g14)
    c: Coincident(g15,g6)
    c: Coincident(g15,g7)
    c: Horizontal(g15)
    c: Horizontal(g14)
    c: Horizontal(g13)
    c: Coincident(g16,g1)
    c: Coincident(g16,g12)
    c: Horizontal(g16)
    c: PointOnObject(g10,g16)
    c: DistanceX(g8,g8) = 2
    c: Equal(g8,g5)
    c: Equal(g5,g11)
    c: Horizontal(g5,g7)
    c: Horizontal(g10,g8)
    c: Coincident(g12,g13)
    c: Symmetric(g2,g0,g-2)
    c: DistanceX(g3,g3) = 20.1
    c: DistanceX(g9,g10) = 7
    c: DistanceX(g6,g7) = 5.5
    c: PointOnObject(g7,g16)
    c: PointOnObject(g9,g-2)
    c: DistanceY(g9,g-1) = 5
    c: DistanceY(g11,g-1) = 12
    c: DistanceY(g2,g2) = 15
FEATURE [PartDesign::Pocket] Pocket099
  BaseFeature = -> Pad120
  Direction = (0,0,-1)
  Length = 7
  Length2 = 5
  Midplane = true
  Profile = -> Sketch245
  ReferenceAxis = -> Sketch245 [N_Axis]
  Suppressed = false
  Type = 0
FEATURE [Part::Part2DObjectPython] Shape2DView004  label="ElevateurCanettes_plaque_interface"  # Draft 2D object (typed FeaturePython)
  AutoUpdate = true
  Base = -> Pocket089
  Clip = false
  FaceNumbers = [4]
  FuseArch = false
  HiddenLines = false
  InPlace = true
  OnlySolids = false
  Projection = (0,-1,0)
  ProjectionMode = 0
  SegmentLength = 0.05
  Tessellation = false
  VisibleOnly = false
FEATURE [Sketcher::SketchObject] Sketch246
  ArcFitTolerance = 1e-06
  AttachmentSupport = -> [YZ_Plane286]
  FullyConstrained = true
  MakeInternals = false
  MapMode = 5
  Placement = pos=(0,0,0) rot=(0.57735,0.57735,0.57735;2.0944rad)
  sketch-geometry (20):
    g0: LineSegment StartX=-18.1 StartY=18.5 StartZ=0 EndX=-18.1 EndY=16.5 EndZ=0
    g1: LineSegment StartX=-16.1 StartY=14.5 StartZ=0 EndX=-10.1 EndY=14.5 EndZ=0
    g2: LineSegment StartX=-8.1 StartY=12.5 StartZ=0 EndX=-8.1 EndY=-4.1 EndZ=0
    g3: LineSegment StartX=-6.1 StartY=-6.1 StartZ=0 EndX=0 EndY=-6.1 EndZ=0
    g4: LineSegment StartX=0 StartY=-6.1 StartZ=0 EndX=0 EndY=-0.1 EndZ=0
    g5: LineSegment StartX=0 StartY=-0.1 StartZ=0 EndX=-6.1 EndY=-0.1 EndZ=0
    g6: LineSegment StartX=-6.1 StartY=-0.1 StartZ=0 EndX=-6.1 EndY=8.1 EndZ=0
    g7: LineSegment StartX=-6.1 StartY=8.1 StartZ=0 EndX=0 EndY=8.1 EndZ=0
    g8: LineSegment StartX=0 StartY=8.1 StartZ=0 EndX=0 EndY=18.5 EndZ=0
    g9: LineSegment StartX=0 StartY=18.5 StartZ=0 EndX=-18.1 EndY=18.5 EndZ=0
    g10: ArcOfCircle CenterX=-10.1 CenterY=12.5 CenterZ=0 NormalX=0 NormalY=0 NormalZ=1 AngleXU=0 Radius=2 StartAngle=-9e-16 EndAngle=1.5708
    g11: GeomPoint [constr] X=-8.1 Y=14.5 Z=0
    g12: ArcOfCircle CenterX=-6.1 CenterY=-4.1 CenterZ=0 NormalX=0 NormalY=0 NormalZ=1 AngleXU=0 Radius=2 StartAngle=3.14159 EndAngle=4.71239
    g13: GeomPoint [constr] X=-8.1 Y=-6.1 Z=0
    g14: ArcOfCircle CenterX=-16.1 CenterY=16.5 CenterZ=0 NormalX=0 NormalY=0 NormalZ=1 AngleXU=0 Radius=2 StartAngle=3.14159 EndAngle=4.71239
    g15: GeomPoint [constr] X=-18.1 Y=14.5 Z=0
    g16: LineSegment [constr] StartX=-6 StartY=8 StartZ=0 EndX=-6 EndY=0 EndZ=0
    g17: LineSegment [constr] StartX=-6 StartY=0 StartZ=0 EndX=0 EndY=0 EndZ=0
    g18: LineSegment [constr] StartX=0 StartY=0 StartZ=0 EndX=0 EndY=8 EndZ=0
    g19: LineSegment [constr] StartX=0 StartY=8 StartZ=0 EndX=-6 EndY=8 EndZ=0
  constraints (53):
    c: Vertical(g0)
    c: Horizontal(g1)
    c: Vertical(g2)
    c: PointOnObject(g3,g-2)
    c: Horizontal(g3)
    c: Coincident(g3,g4)
    c: PointOnObject(g4,g-2)
    c: Coincident(g4,g5)
    c: Horizontal(g5)
    c: Vertical(g6)
    c: Coincident(g6,g7)
    c: Horizontal(g7)
    c: Coincident(g7,g8)
    c: Vertical(g8)
    c: Coincident(g8,g9)
    c: Coincident(g9,g0)
    c: Horizontal(g9)
    c: PointOnObject(g7,g-2)
    c: PointOnObject(g11,g1)
    c: PointOnObject(g11,g2)
    c: Tangent(g1,g10) = 1.5708
    c: Tangent(g2,g10) = 1.5708
    c: PointOnObject(g13,g3)
    c: PointOnObject(g13,g2)
    c: Tangent(g3,g12) = -1.5708
    c: Tangent(g2,g12) = -1.5708
    c: PointOnObject(g15,g1)
    c: PointOnObject(g15,g0)
    c: Tangent(g1,g14) = -1.5708
    c: Tangent(g0,g14) = -1.5708
    c: DistanceY(g1,g0) = 4
    c: DistanceX(g0,g2) = 10
    c: Equal(g14,g10)
    c: Radius(g14) = 2
    c: Coincident(g16,g17)
    c: Coincident(g17,g18)
    c: Coincident(g18,g19)
    c: Coincident(g19,g16)
    c: Vertical(g16)
    c: Vertical(g18)
    c: Horizontal(g17)
    c: Horizontal(g19)
    c: Coincident(g17,g-1)
    c: DistanceX(g6,g16) = 0.1
    c: DistanceY(g18,g7) = 0.1
    c: DistanceX(g17,g17) = 6
    c: DistanceY(g18,g18) = 8
    c: DistanceY(g-1,g8) = 18.5
    c: DistanceY(g4,g4) = 6
    c: DistanceY(g4,g17) = 0.1
    c: Coincident(g5,g6)
    c: Vertical(g12,g5)
    c: Radius(g12) = 2
FEATURE [PartDesign::Pad] Pad121
  Direction = (1,0,0)
  Length = 20
  Length2 = 10
  Midplane = true
  Placement = pos=(0,0,0) rot=(1,1,1;2.0944rad)
  Profile = -> Sketch246
  ReferenceAxis = -> Sketch246 [N_Axis]
  Suppressed = false
  Type = 0
FEATURE [Sketcher::SketchObject] Sketch247
  ArcFitTolerance = 1e-06
  AttachmentSupport = -> [XY_Plane286]
  ExternalGeometry = -> [Pad121]
  FullyConstrained = true
  MakeInternals = false
  MapMode = 5
  Placement = pos=(0,0,0) rot=(0,1,0;3.14159rad)
  sketch-geometry (8):
    g0: Circle CenterX=-4 CenterY=-13.1 CenterZ=0 NormalX=0 NormalY=0 NormalZ=1 AngleXU=0 Radius=2.75
    g1: LineSegment [constr] StartX=-4 StartY=-10.1 StartZ=0 EndX=-4 EndY=-16.1 EndZ=0
    g2: LineSegment StartX=1 StartY=-13.1 StartZ=0 EndX=1 EndY=-18.1 EndZ=0
    g3: LineSegment StartX=1 StartY=-18.1 StartZ=0 EndX=10 EndY=-18.1 EndZ=0
    g4: LineSegment StartX=10 StartY=-18.1 StartZ=0 EndX=10 EndY=-10.1 EndZ=0
    g5: LineSegment StartX=10 StartY=-10.1 StartZ=0 EndX=4 EndY=-10.1 EndZ=0
    g6: ArcOfCircle CenterX=4 CenterY=-13.1 CenterZ=0 NormalX=0 NormalY=0 NormalZ=1 AngleXU=0 Radius=3 StartAngle=1.5708 EndAngle=3.14159
    g7: GeomPoint [constr] X=1 Y=-10.1 Z=0
  constraints (21):
    c: PointOnObject(g1,g-3)
    c: PointOnObject(g1,g-4)
    c: Perpendicular(g-3,g1)
    c: Symmetric(g1,g1,g0)
    c: DistanceX(g0,g-1) = 4
    c: Diameter(g0) = 5.5
    c: Coincident(g2,g3)
    c: Coincident(g3,g4)
    c: Coincident(g4,g5)
    c: Vertical(g2)
    c: Vertical(g4)
    c: Horizontal(g3)
    c: Horizontal(g5)
    c: Coincident(g3,g-5)
    c: PointOnObject(g7,g5)
    c: PointOnObject(g7,g2)
    c: Tangent(g5,g6) = -1.5708
    c: Tangent(g2,g6) = -1.5708
    c: PointOnObject(g7,g-3)
    c: Radius(g6) = 3
    c: DistanceX(g0,g2) = 5
FEATURE [PartDesign::Pocket] Pocket100
  BaseFeature = -> Pad121
  Direction = (0,0,1)
  Length = 5
  Length2 = 5
  Placement = pos=(0,0,0) rot=(1,1,1;2.0944rad)
  Profile = -> Sketch247
  ReferenceAxis = -> Sketch247 [N_Axis]
  Suppressed = false
  Type = 1
FEATURE [Sketcher::SketchObject] Sketch248
  ArcFitTolerance = 1e-06
  AttachmentOffset = pos=(0,0,-6) rot=(0,0,1;0rad)
  AttachmentSupport = -> [Pocket100]
  FullyConstrained = true
  MakeInternals = false
  MapMode = 5
  Placement = pos=(0,-1.3e-15,-0.1) rot=(0.707107,0.707107,0;3.14159rad)
  sketch-geometry (1):
    g0: Circle CenterX=0 CenterY=-1 CenterZ=0 NormalX=0 NormalY=0 NormalZ=1 AngleXU=0 Radius=2.1
  constraints (3):
    c: Diameter(g0) = 4.2
    c: PointOnObject(g0,g-2)
    c: DistanceY(g0,g-1) = 1
FEATURE [PartDesign::Pocket] Pocket101
  BaseFeature = -> Pocket100
  Direction = (0,0,1)
  Length = 16
  Length2 = 5
  Placement = pos=(0,0,0) rot=(1,1,1;2.0944rad)
  Profile = -> Sketch248
  ReferenceAxis = -> Sketch248 [N_Axis]
  Reversed = true
  Suppressed = false
  Type = 0
FEATURE [Sketcher::SketchObject] Sketch249
  ArcFitTolerance = 1e-06
  AttachmentSupport = -> [XZ_Plane286]
  ExternalGeometry = -> [Pocket101]
  FullyConstrained = true
  MakeInternals = false
  MapMode = 5
  Placement = pos=(0,0,0) rot=(1,0,0;1.5708rad)
  sketch-geometry (9):
    g0: LineSegment StartX=-10 StartY=18.5 StartZ=0 EndX=-2 EndY=18.5 EndZ=0
    g1: LineSegment StartX=-2 StartY=18.5 StartZ=0 EndX=-2 EndY=8.1 EndZ=0
    g2: LineSegment StartX=-2 StartY=8.1 StartZ=0 EndX=-10 EndY=8.1 EndZ=0
    g3: LineSegment StartX=-10 StartY=8.1 StartZ=0 EndX=-10 EndY=18.5 EndZ=0
    g4: GeomPoint [constr] X=-2 Y=8.1 Z=0
    g5: LineSegment StartX=10 StartY=-6.1 StartZ=0 EndX=10 EndY=18.5 EndZ=0
    g6: LineSegment StartX=8 StartY=18.5 StartZ=0 EndX=2 EndY=-6.1 EndZ=0
    g7: LineSegment StartX=2 StartY=-6.1 StartZ=0 EndX=10 EndY=-6.1 EndZ=0
    g8: LineSegment StartX=8 StartY=18.5 StartZ=0 EndX=10 EndY=18.5 EndZ=0
  constraints (22):
    c: Coincident(g0,g1)
    c: Coincident(g2,g3)
    c: Horizontal(g0)
    c: Horizontal(g2)
    c: Coincident(g2,g-6)
    c: Coincident(g0,g3)
    c: Coincident(g0,g-6)
    c: Vertical(g1)
    c: DistanceX(g4,g-1) = 2
    c: Coincident(g1,g2)
    c: Coincident(g1,g4)
    c: Coincident(g6,g7)
    c: Coincident(g7,g5)
    c: Horizontal(g7)
    c: Coincident(g5,g-4)
    c: DistanceX(g7,g7) = 8
    c: Coincident(g8,g6)
    c: Coincident(g8,g5)
    c: Vertical(g5,g-3)
    c: Horizontal(g8)
    c: Horizontal(g6,g0)
    c: DistanceX(g8,g8) = 2
FEATURE [PartDesign::Pocket] Pocket102
  BaseFeature = -> Pocket101
  Direction = (0,1,-2e-16)
  Length = 5
  Length2 = 5
  Midplane = true
  Placement = pos=(0,0,0) rot=(1,1,1;2.0944rad)
  Profile = -> Sketch249
  ReferenceAxis = -> Sketch249 [N_Axis]
  Suppressed = false
  Type = 1
FEATURE [PartDesign::Mirrored] Mirrored011
  BaseFeature = -> Pocket102
  MirrorPlane = -> XZ_Plane286
  Originals = -> [Pocket102]
  Placement = pos=(0,0,0) rot=(1,1,1;2.0944rad)
  Refine = true
  Suppressed = false
  TransformMode = 1
FEATURE [Sketcher::SketchObject] Sketch251
  ArcFitTolerance = 1e-06
  AttachmentOffset = pos=(12,-4,-20) rot=(0,0,-1;1.5708rad)
  AttachmentSupport = -> [XZ_Plane274]
  FullyConstrained = true
  MakeInternals = false
  MapMode = 5
  Placement = pos=(12,20,-4) rot=(0.57735,0.57735,-0.57735;2.0944rad)
  sketch-geometry (10):
    g0: LineSegment StartX=-11 StartY=3.7 StartZ=0 EndX=-11 EndY=-5 EndZ=0
    g1: LineSegment StartX=-10 StartY=-6 StartZ=0 EndX=10 EndY=-6 EndZ=0
    g2: LineSegment StartX=11 StartY=-5 StartZ=0 EndX=11 EndY=3.7 EndZ=0
    g3: LineSegment StartX=10 StartY=4.7 StartZ=0 EndX=-10 EndY=4.7 EndZ=0
    g4: ArcOfCircle CenterX=-10 CenterY=3.7 CenterZ=0 NormalX=0 NormalY=0 NormalZ=1 AngleXU=0 Radius=1 StartAngle=1.5708 EndAngle=3.14159
    g5: ArcOfCircle CenterX=-10 CenterY=-5 CenterZ=0 NormalX=0 NormalY=0 NormalZ=1 AngleXU=0 Radius=1 StartAngle=3.14159 EndAngle=4.71239
    g6: ArcOfCircle CenterX=10 CenterY=-5 CenterZ=0 NormalX=0 NormalY=0 NormalZ=1 AngleXU=0 Radius=1 StartAngle=4.71239 EndAngle=6.28319
    g7: ArcOfCircle CenterX=10 CenterY=3.7 CenterZ=0 NormalX=0 NormalY=0 NormalZ=1 AngleXU=0 Radius=1 StartAngle=0 EndAngle=1.5708
    g8: GeomPoint [constr] X=-11 Y=4.7 Z=0
    g9: GeomPoint [constr] X=11 Y=-6 Z=0
  constraints (23):
    c: Tangent(g0,g4) = -1.5708
    c: Tangent(g0,g5) = -1.5708
    c: Tangent(g1,g5) = -1.5708
    c: Tangent(g1,g6) = -1.5708
    c: Tangent(g2,g6) = -1.5708
    c: Tangent(g2,g7) = -1.5708
    c: Tangent(g3,g7) = -1.5708
    c: Tangent(g3,g4) = -1.5708
    c: Vertical(g0)
    c: Vertical(g2)
    c: Horizontal(g3)
    c: Equal(g4,g5)
    c: Equal(g5,g6)
    c: Equal(g6,g7)
    c: PointOnObject(g8,g0)
    c: PointOnObject(g8,g3)
    c: PointOnObject(g9,g1)
    c: PointOnObject(g9,g2)
    c: Radius(g4) = 1
    c: DistanceX(g0,g2) = 22
    c: DistanceY(g1,g-1) = 6
    c: Symmetric(g1,g1,g-2)
    c: DistanceY(g-1,g2) = 3.7
FEATURE [Sketcher::SketchObject] Sketch252
  ArcFitTolerance = 1e-06
  AttachmentOffset = pos=(12,-4,-20) rot=(0,0,-1;1.5708rad)
  AttachmentSupport = -> [XZ_Plane274]
  FullyConstrained = true
  MakeInternals = false
  MapMode = 5
  Placement = pos=(12,20,-4) rot=(0.57735,0.57735,-0.57735;2.0944rad)
  sketch-geometry (17):
    g0: LineSegment StartX=-10.15 StartY=10 StartZ=0 EndX=-10.15 EndY=-5 EndZ=0
    g1: LineSegment StartX=-10.15 StartY=-5 StartZ=0 EndX=-9.5 EndY=-5 EndZ=0
    g2: LineSegment StartX=10.15 StartY=-5 StartZ=0 EndX=10.15 EndY=10 EndZ=0
    g3: LineSegment StartX=10.15 StartY=10 StartZ=0 EndX=-10.15 EndY=10 EndZ=0
    g4: LineSegment StartX=-9.5 StartY=-5 StartZ=0 EndX=-9.5 EndY=-9 EndZ=0
    g5: LineSegment StartX=-9.5 StartY=-9 StartZ=0 EndX=-7.5 EndY=-9 EndZ=0
    g6: LineSegment StartX=-7.5 StartY=-9 StartZ=0 EndX=-7.5 EndY=-5 EndZ=0
    g7: LineSegment StartX=-2 StartY=-5 StartZ=0 EndX=-2 EndY=-9 EndZ=0
    g8: LineSegment StartX=-2 StartY=-9 StartZ=0 EndX=0 EndY=-9 EndZ=0
    g9: LineSegment StartX=0 StartY=-9 StartZ=0 EndX=0 EndY=-5 EndZ=0
    g10: LineSegment StartX=7 StartY=-5 StartZ=0 EndX=7 EndY=-9 EndZ=0
    g11: LineSegment StartX=7 StartY=-9 StartZ=0 EndX=9 EndY=-9 EndZ=0
    g12: LineSegment StartX=9 StartY=-9 StartZ=0 EndX=9 EndY=-5 EndZ=0
    g13: LineSegment StartX=9 StartY=-5 StartZ=0 EndX=10.15 EndY=-5 EndZ=0
    g14: LineSegment StartX=0 StartY=-5 StartZ=0 EndX=7 EndY=-5 EndZ=0
    g15: LineSegment StartX=-7.5 StartY=-5 StartZ=0 EndX=-2 EndY=-5 EndZ=0
    g16: LineSegment [constr] StartX=-9.5 StartY=-5 StartZ=0 EndX=9 EndY=-5 EndZ=0
  constraints (49):
    c: Coincident(g0,g1)
    c: Coincident(g13,g2)
    c: Coincident(g2,g3)
    c: Coincident(g3,g0)
    c: Vertical(g0)
    c: Vertical(g2)
    c: Horizontal(g1)
    c: Coincident(g4,g5)
    c: Coincident(g5,g6)
    c: Vertical(g4)
    c: Vertical(g6)
    c: Horizontal(g5)
    c: Coincident(g7,g8)
    c: Coincident(g8,g9)
    c: Vertical(g7)
    c: Vertical(g9)
    c: Horizontal(g8)
    c: Coincident(g10,g11)
    c: Coincident(g11,g12)
    c: Vertical(g10)
    c: Vertical(g12)
    c: Horizontal(g11)
    c: Coincident(g1,g4)
    c: Coincident(g14,g10)
    c: Coincident(g9,g14)
    c: Coincident(g15,g6)
    c: Coincident(g15,g7)
    c: Horizontal(g15)
    c: Horizontal(g14)
    c: Horizontal(g13)
    c: Coincident(g16,g1)
    c: Coincident(g16,g12)
    c: Horizontal(g16)
    c: PointOnObject(g10,g16)
    c: DistanceX(g8,g8) = 2
    c: Equal(g8,g5)
    c: Equal(g5,g11)
    c: Horizontal(g5,g7)
    c: Horizontal(g10,g8)
    c: Coincident(g12,g13)
    c: Symmetric(g2,g0,g-2)
    c: DistanceX(g3,g3) = 20.3
    c: DistanceX(g9,g10) = 7
    c: DistanceX(g6,g7) = 5.5
    c: PointOnObject(g7,g16)
    c: PointOnObject(g9,g-2)
    c: DistanceY(g9,g-1) = 5
    c: DistanceY(g11,g-1) = 9
    c: DistanceY(g2,g2) = 15
FEATURE [Part::FeaturePython] Screw002  label="M3x16-Vis001"  # WARN: FeaturePython — macro-defined, semantics opaque (R4)
  Diameter = 4
  Invert = false
  LeftHanded = false
  Length = 6
  LengthCustom = 16
  MatchOuter = false
  OffsetAngle = 0
  Placement = pos=(3,-20,-11) rot=(-0.707107,0,-0.707107;3.14159rad)
  Thread = false
  Type = 75
FEATURE [PartDesign::Mirrored] Mirrored
  BaseFeature = -> Pocket086
  MirrorPlane = -> YZ_Plane275
  Placement = pos=(0,0,0) rot=(1,0,0;1.5708rad)
  Suppressed = false
  TransformMode = 1
FEATURE [Sketcher::SketchObject] Sketch253
  ArcFitTolerance = 1e-06
  AttachmentSupport = -> [Pocket099]
  ExternalGeometry = -> [Pocket099]
  FullyConstrained = true
  MakeInternals = false
  MapMode = 5
  Placement = pos=(-11,0,0) rot=(0.57735,0.57735,0.57735;2.0944rad)
  sketch-geometry (13):
    g0: ArcOfCircle CenterX=-10 CenterY=-11 CenterZ=0 NormalX=0 NormalY=0 NormalZ=1 AngleXU=0 Radius=1.75 StartAngle=1.5708 EndAngle=4.71239
    g1: LineSegment StartX=-10 StartY=-9.25 StartZ=0 EndX=0 EndY=-9.25 EndZ=0
    g2: LineSegment StartX=-10 StartY=-12.75 StartZ=0 EndX=0 EndY=-12.75 EndZ=0
    g3: LineSegment StartX=-14 StartY=-8.7651 StartZ=0 EndX=-14 EndY=-12.75 EndZ=0
    g4: LineSegment StartX=-12 StartY=-14.75 StartZ=0 EndX=0 EndY=-14.75 EndZ=0
    g5: LineSegment StartX=0 StartY=-5 StartZ=0 EndX=-6 EndY=-5 EndZ=0
    g6: LineSegment StartX=-12.5415 StartY=-6.83979 StartZ=0 EndX=-6 EndY=-5 EndZ=0
    g7: LineSegment StartX=0 StartY=-9.25 StartZ=0 EndX=0 EndY=-5 EndZ=0
    g8: LineSegment StartX=0 StartY=-14.75 StartZ=0 EndX=0 EndY=-12.75 EndZ=0
    g9: ArcOfCircle CenterX=-12 CenterY=-8.7651 CenterZ=0 NormalX=0 NormalY=0 NormalZ=1 AngleXU=0 Radius=2 StartAngle=1.84496 EndAngle=3.14159
    g10: GeomPoint [constr] X=-14 Y=-7.25 Z=0
    g11: ArcOfCircle CenterX=-12 CenterY=-12.75 CenterZ=0 NormalX=0 NormalY=0 NormalZ=1 AngleXU=0 Radius=2 StartAngle=3.14159 EndAngle=4.71239
    g12: GeomPoint [constr] X=-14 Y=-14.75 Z=0
  constraints (33):
    c: Tangent(g0,g1) = 1.5708
    c: Tangent(g0,g2) = -1.5708
    c: Radius(g0) = 1.75
    c: Vertical(g3)
    c: Horizontal(g5)
    c: Coincident(g6,g-3)
    c: PointOnObject(g4,g-2)
    c: PointOnObject(g2,g-2)
    c: PointOnObject(g1,g-2)
    c: Coincident(g7,g1)
    c: Coincident(g8,g4)
    c: Coincident(g8,g2)
    c: Coincident(g5,g7)
    c: Vertical(g7)
    c: Horizontal(g1)
    c: Horizontal(g2)
    c: DistanceX(g0,g-1) = 10
    c: Horizontal(g4)
    c: DistanceY(g8,g8) = 2
    c: DistanceY(g0,g-1) = 11
    c: DistanceY(g0,g10) = 2
    c: PointOnObject(g10,g6)
    c: PointOnObject(g10,g3)
    c: Tangent(g6,g9) = 1.5708
    c: Tangent(g3,g9) = -1.5708
    c: PointOnObject(g12,g3)
    c: PointOnObject(g12,g4)
    c: Tangent(g3,g11) = -1.5708
    c: Tangent(g4,g11) = -1.5708
    c: Horizontal(g11,g0)
    c: Vertical(g9,g11)
    c: DistanceX(g3,g-1) = 14
    c: Coincident(g5,g6)
FEATURE [PartDesign::Pad] Pad124
  BaseFeature = -> Pocket099
  Direction = (1,0,0)
  Length = 9
  Length2 = 10
  Profile = -> Sketch253
  ReferenceAxis = -> Sketch253 [N_Axis]
  Suppressed = false
  Type = 0
FEATURE [PartDesign::Mirrored] Mirrored012
  BaseFeature = -> Pad124
  MirrorPlane = -> Sketch253 [V_Axis]
  Originals = -> [Pad124]
  Suppressed = false
  TransformMode = 0
FEATURE [PartDesign::Body] Body087  label="support_micro_switch"
  AllowCompound = false
  Group = -> [Sketch244,Pad120,Sketch245,Pocket099,Sketch253,Pad124,Mirrored012]
  Origin = -> Origin288
  Placement = pos=(0,0,-5.53e-14) rot=(-0.57735,0.57735,0.57735;2.0944rad)
  Tip = -> Mirrored012
FEATURE [App::Part] Part002009  label="micro_switch_haut"
  Group = -> [Body087,Link005]
  Origin = -> Origin290
  Placement = pos=(160,11,-11) rot=(0,0,1;0rad)
FEATURE [Sketcher::SketchObject] Sketch254
  ArcFitTolerance = 1e-06
  AttachmentSupport = -> [XZ_Plane275]
  ExternalGeometry = -> [Mirrored]
  FullyConstrained = true
  MakeInternals = false
  MapMode = 5
  Placement = pos=(0,0,0) rot=(1,0,0;1.5708rad)
  sketch-geometry (17):
    g0: LineSegment StartX=8 StartY=-6 StartZ=0 EndX=24.4218 EndY=-23.7533 EndZ=0
    g1: LineSegment StartX=29.5605 StartY=-26 StartZ=0 EndX=30 EndY=-26 EndZ=0
    g2: LineSegment StartX=31.5 StartY=-24.5 StartZ=0 EndX=31.5 EndY=-15.5 EndZ=0
    g3: LineSegment StartX=29.5605 StartY=-14 StartZ=0 EndX=30 EndY=-14 EndZ=0
    g4: ArcOfCircle CenterX=8 CenterY=-4 CenterZ=0 NormalX=0 NormalY=0 NormalZ=1 AngleXU=0 Radius=2 StartAngle=4.71239 EndAngle=6.28319
    g5: LineSegment StartX=10 StartY=-4 StartZ=0 EndX=10 EndY=1.8e-15 EndZ=0
    g6: LineSegment StartX=10 StartY=1.8e-15 StartZ=0 EndX=13.55 EndY=0 EndZ=0
    g7: LineSegment StartX=13.55 StartY=0 StartZ=0 EndX=24.4218 EndY=-11.7533 EndZ=0
    g8: Circle CenterX=20 CenterY=-11 CenterZ=0 NormalX=0 NormalY=0 NormalZ=1 AngleXU=0 Radius=2.1
    g9: ArcOfCircle CenterX=29.5605 CenterY=-7 CenterZ=0 NormalX=0 NormalY=0 NormalZ=1 AngleXU=0 Radius=7 StartAngle=3.88805 EndAngle=4.71239
    g10: GeomPoint [constr] X=26.5 Y=-14 Z=0
    g11: ArcOfCircle CenterX=29.5605 CenterY=-19 CenterZ=0 NormalX=0 NormalY=0 NormalZ=1 AngleXU=0 Radius=7 StartAngle=3.88805 EndAngle=4.71239
    g12: GeomPoint [constr] X=26.5 Y=-26 Z=0
    g13: ArcOfCircle CenterX=30 CenterY=-15.5 CenterZ=0 NormalX=0 NormalY=0 NormalZ=1 AngleXU=0 Radius=1.5 StartAngle=3e-16 EndAngle=1.5708
    g14: GeomPoint [constr] X=31.5 Y=-14 Z=0
    g15: ArcOfCircle CenterX=30 CenterY=-24.5 CenterZ=0 NormalX=0 NormalY=0 NormalZ=1 AngleXU=0 Radius=1.5 StartAngle=4.71239 EndAngle=6.28319
    g16: GeomPoint [constr] X=31.5 Y=-26 Z=0
  constraints (41):
    c: Horizontal(g1)
    c: Coincident(g4,g-4)
    c: Coincident(g4,g-4)
    c: Coincident(g5,g4)
    c: Coincident(g5,g-3)
    c: Vertical(g5)
    c: Coincident(g6,g5)
    c: PointOnObject(g6,g-1)
    c: Coincident(g7,g6)
    c: Coincident(g0,g4)
    c: Vertical(g2)
    c: Horizontal(g3)
    c: Diameter(g8) = 4.2
    c: DistanceX(g-1,g8) = 20
    c: DistanceY(g8,g-1) = 11
    c: Parallel(g7,g0)
    c: Vertical(g10,g12)
    c: DistanceX(g-1,g14) = 31.5
    c: DistanceY(g14,g-1) = 14
    c: DistanceY(g16,g14) = 12
    c: DistanceX(g12,g16) = 5
    c: PointOnObject(g10,g7)
    c: PointOnObject(g10,g3)
    c: Tangent(g7,g9) = -1.5708
    c: Tangent(g3,g9) = -1.5708
    c: PointOnObject(g12,g0)
    c: PointOnObject(g12,g1)
    c: Tangent(g0,g11) = -1.5708
    c: Tangent(g1,g11) = -1.5708
    c: Radius(g9) = 7
    c: Equal(g9,g11)
    c: PointOnObject(g14,g3)
    c: PointOnObject(g14,g2)
    c: Tangent(g3,g13) = 1.5708
    c: Tangent(g2,g13) = -1.5708
    c: PointOnObject(g16,g1)
    c: PointOnObject(g16,g2)
    c: Tangent(g1,g15) = -1.5708
    c: Tangent(g2,g15) = -1.5708
    c: Equal(g13,g15)
    c: Radius(g13) = 1.5
FEATURE [PartDesign::Pad] Pad125
  BaseFeature = -> Mirrored
  Direction = (0,-1,2e-16)
  Length = 6
  Length2 = 10
  Midplane = true
  Placement = pos=(0,0,0) rot=(1,0,0;1.5708rad)
  Profile = -> Sketch254
  ReferenceAxis = -> Sketch254 [N_Axis]
  Suppressed = false
  Type = 0
FEATURE [PartDesign::Body] Body079  label="bras_fin_course"
  AllowCompound = false
  Group = -> [Sketch214,Pad106,Sketch216,Pocket086,Mirrored,Sketch254,Pad125]
  Origin = -> Origin278
  Placement = pos=(0,0,0) rot=(0,0,-1;1.5708rad)
  Tip = -> Pad125
FEATURE [App::Part] Part002010  label="bras_fin_de_course"
  Group = -> [Body079,Screw002]
  Origin = -> Origin291
  Placement = pos=(10,40,13) rot=(0,0,1;0rad)
FEATURE [Sketcher::SketchObject] Sketch255
  ArcFitTolerance = 1e-06
  AttachmentOffset = pos=(0,0,-15) rot=(0,0,1;0rad)
  AttachmentSupport = -> [XZ_Plane274]
  FullyConstrained = true
  MakeInternals = false
  MapMode = 5
  Placement = pos=(0,15,-3.3e-15) rot=(1,0,0;1.5708rad)
  sketch-geometry (4):
    g0: LineSegment StartX=-2 StartY=-2.039 StartZ=0 EndX=7.039 EndY=7 EndZ=0
    g1: LineSegment StartX=-2 StartY=-5.961 StartZ=0 EndX=7.039 EndY=-15 EndZ=0
    g2: LineSegment StartX=-2 StartY=-2.039 StartZ=0 EndX=-2 EndY=-5.961 EndZ=0
    g3: LineSegment StartX=7.039 StartY=7 StartZ=0 EndX=7.039 EndY=-15 EndZ=0
  constraints (12):
    c: Coincident(g2,g0)
    c: Coincident(g2,g1)
    c: Vertical(g2)
    c: Coincident(g3,g0)
    c: Vertical(g3)
    c: Coincident(g1,g3)
    c: Angle(g2,g1) = 0.785398
    c: DistanceY(g3,g3) = 22
    c: DistanceY(g-1,g0) = 7
    c: Angle(g0,g2) = 0.785398
    c: DistanceX(g-1,g0) = 7.039
    c: DistanceX(g0,g-1) = 2
FEATURE [PartDesign::Pad] Pad126
  BaseFeature = -> Pocket090
  Direction = (0,-1,2e-16)
  Length = 1.5
  Length2 = 10
  Placement = pos=(0,0,0) rot=(1,1,1;2.0944rad)
  Profile = -> Sketch255
  ReferenceAxis = -> Sketch255 [N_Axis]
  Reversed = true
  Suppressed = false
  Type = 0
FEATURE [PartDesign::LinearPattern] LinearPattern005
  BaseFeature = -> Pad126
  Direction = -> Sketch255 [N_Axis]
  Length = 8.5
  Mode = 0
  Occurrences = 2
  Offset = 8.5
  Originals = -> [Pad126]
  Placement = pos=(0,0,0) rot=(1,1,1;2.0944rad)
  Reversed = true
  Suppressed = false
  TransformMode = 0
FEATURE [PartDesign::Pad] Pad123  label="micro_switch002"
  BaseFeature = -> LinearPattern005
  Direction = (0,-1,2e-16)
  Length = 10
  Length2 = 10
  Midplane = true
  Placement = pos=(0,0,0) rot=(1,1,1;2.0944rad)
  Profile = -> Sketch251
  ReferenceAxis = -> Sketch251 [N_Axis]
  Suppressed = false
  Type = 0
FEATURE [PartDesign::Pocket] Pocket103  label="micro_switch003"
  BaseFeature = -> Pad123
  Direction = (0,1,-2e-16)
  Length = 7
  Length2 = 5
  Midplane = true
  Placement = pos=(0,0,0) rot=(1,1,1;2.0944rad)
  Profile = -> Sketch252
  ReferenceAxis = -> Sketch252 [N_Axis]
  Suppressed = false
  Type = 0
FEATURE [PartDesign::Body] Body078  label="support_rail_bas"
  AllowCompound = false
  Group = -> [Sketch208,Pad102,Sketch209,Pad103,Sketch210,Pad104,Fillet,Mirrored005,Sketch211,Pocket083,Sketch212,Pad105,Chamfer,Mirrored006,Sketch213,Pocket084,Sketch224,Pocket090,Sketch255,Pad126,LinearPattern005,Sketch251,Sketch252,Pad123,Pocket103]
  Origin = -> Origin277
  Placement = pos=(0,0,4) rot=(0,0,1;0rad)
  Tip = -> Pocket103
FEATURE [App::Link] Link006  label="DA20_spacer001"
  LinkPlacement = pos=(0,0,20) rot=(0,1,0;3.14159rad)
  LinkTransform = true
  LinkedObject = -> Body075
  Placement = pos=(0,0,20) rot=(0,1,0;3.14159rad)
FEATURE [Sketcher::SketchObject] Sketch256
  ArcFitTolerance = 1e-06
  AttachmentSupport = -> [XY_Plane271]
  FullyConstrained = true
  MakeInternals = false
  MapMode = 5
  sketch-geometry (4):
    g0: LineSegment StartX=-10 StartY=-4 StartZ=0 EndX=10 EndY=-4 EndZ=0
    g1: LineSegment StartX=10 StartY=-4 StartZ=0 EndX=10 EndY=-2 EndZ=0
    g2: LineSegment StartX=10 StartY=-2 StartZ=0 EndX=-10 EndY=-2 EndZ=0
    g3: LineSegment StartX=-10 StartY=-2 StartZ=0 EndX=-10 EndY=-4 EndZ=0
  constraints (11):
    c: Coincident(g0,g1)
    c: Coincident(g1,g2)
    c: Coincident(g2,g3)
    c: Coincident(g3,g0)
    c: Horizontal(g0)
    c: Vertical(g1)
    c: Vertical(g3)
    c: DistanceX(g2,g2) = 20
    c: Symmetric(g1,g2,g-2)
    c: DistanceY(g0,g-1) = 4
    c: Distance(g1,g-1) = 2
FEATURE [PartDesign::Pocket] Pocket104
  BaseFeature = -> Pad097
  Direction = (0,0,-1)
  Length = 5
  Length2 = 5
  Midplane = true
  Profile = -> Sketch256
  ReferenceAxis = -> Sketch256 [N_Axis]
  Suppressed = false
  Type = 1
FEATURE [PartDesign::Body] Body075  label="DA20_spacer"
  AllowCompound = false
  Group = -> [Sketch198,Pad097,Sketch256,Pocket104]
  Origin = -> Origin274
  Placement = pos=(0,4.5,35) rot=(0,-0.707107,0.707107;3.14159rad)
  Tip = -> Pocket104
FEATURE [App::Part] DA_20_servo_with_attachment_parts  label="DA 20_servo with attachment parts"
  Group = -> [Part__Feature001,Part__Feature002,Part__Feature003,Part__Feature004,Part__Feature005,Plane,Plane003,Slice001,Slice_child1,Slice_child0,Slice,Slice001_child1,Slice001_child0,Body,Body001,Body002,Part,Body075,Body076,Nut,Screw,Link006]
  Origin = -> Origin269
  Placement = pos=(39,-31,6.6) rot=(0,-0.707107,0.707107;3.14159rad)
FEATURE [App::Part] Part002006  label="partie_mobile"
  Group = -> [MGN12H001,DA_20_servo_with_attachment_parts,Body072,Body074,Link,Part002010]
  Origin = -> Origin271
  Placement = pos=(137,0,0) rot=(0,0,1;0rad)
  expr: .Placement.Base.x = 13 mm + VarSet.Position_elevateur_canette
FEATURE [Part::FeaturePython] Screw003  label="M3x8-Vis"  # WARN: FeaturePython — macro-defined, semantics opaque (R4)
  Diameter = 4
  Invert = false
  LeftHanded = false
  Length = 2
  LengthCustom = 8
  MatchOuter = false
  OffsetAngle = 0
  Placement = pos=(-28,-2,2) rot=(0,0,1;0rad)
  Thread = false
  Type = 75
FEATURE [PartDesign::Chamfer] Chamfer007
  Angle = 45
  Base = -> Mirrored011 [Edge81]
  BaseFeature = -> Mirrored011
  ChamferType = 0
  FlipDirection = false
  Placement = pos=(0,0,0) rot=(1,1,1;2.0944rad)
  Size = 1
  Size2 = 1
  SupportTransform = false
  Suppressed = false
  UseAllEdges = false
FEATURE [PartDesign::Body] Body088  label="support_rail_haut"
  AllowCompound = false
  Group = -> [Sketch246,Pad121,Sketch247,Pocket100,Sketch248,Pocket101,Sketch249,Pocket102,Mirrored011,Chamfer007]
  Origin = -> Origin289
  Placement = pos=(211,0,0) rot=(1,0,0;0rad)
  Tip = -> Chamfer007
FEATURE [Sketcher::SketchObject] Sketch257
  ArcFitTolerance = 1e-06
  AttachmentSupport = -> [YZ_Plane289]
  FullyConstrained = true
  MakeInternals = false
  MapMode = 5
  Placement = pos=(0,0,0) rot=(0.57735,0.57735,0.57735;2.0944rad)
  sketch-geometry (4):
    g0: LineSegment StartX=0 StartY=13 StartZ=0 EndX=-148.591 EndY=0 EndZ=0
    g1: LineSegment StartX=-148.591 StartY=0 StartZ=0 EndX=30 EndY=0 EndZ=0
    g2: LineSegment StartX=0 StartY=13 StartZ=0 EndX=30 EndY=13 EndZ=0
    g3: LineSegment StartX=30 StartY=13 StartZ=0 EndX=30 EndY=0 EndZ=0
  constraints (13):
    c: PointOnObject(g0,g-2)
    c: PointOnObject(g0,g-1)
    c: Coincident(g1,g0)
    c: DistanceY(g-1,g0) = 13
    c: Angle(g1,g0) = 0.0872665
    c: Coincident(g2,g0)
    c: Horizontal(g2)
    c: Coincident(g3,g2)
    c: PointOnObject(g3,g-1)
    c: Coincident(g1,g3)
    c: Vertical(g3)
    c: DistanceX(g2,g2) = 30
    c: DistanceX(g0,g1) = 178.591
FEATURE [PartDesign::Pad] Pad127
  Direction = (1,0,0)
  Length = 20
  Length2 = 10
  Midplane = true
  Placement = pos=(0,0,0) rot=(1,1,1;2.0944rad)
  Profile = -> Sketch257
  ReferenceAxis = -> Sketch257 [N_Axis]
  Suppressed = false
  Type = 0
FEATURE [PartDesign::Fillet] Fillet002
  Base = -> Pad127 [Edge10,Edge9]
  BaseFeature = -> Pad127
  Placement = pos=(0,0,0) rot=(1,1,1;2.0944rad)
  Radius = 8
  SupportTransform = false
  Suppressed = false
  UseAllEdges = false
FEATURE [Sketcher::SketchObject] Sketch258
  ArcFitTolerance = 1e-06
  AttachmentSupport = -> [Fillet002]
  ExternalGeometry = -> [Fillet002]
  FullyConstrained = true
  MakeInternals = false
  MapMode = 5
  Placement = pos=(-1.4e-15,4.3e-15,13) rot=(0,0,-1;1.5708rad)
  sketch-geometry (7):
    g0: ArcOfCircle CenterX=-15.7047 CenterY=0 CenterZ=0 NormalX=0 NormalY=0 NormalZ=1 AngleXU=0 Radius=8 StartAngle=1.5708 EndAngle=4.71239
    g1: ArcOfCircle CenterX=134.295 CenterY=4e-16 CenterZ=0 NormalX=0 NormalY=0 NormalZ=1 AngleXU=0 Radius=8 StartAngle=4.71239 EndAngle=7.85398
    g2: LineSegment StartX=-15.7047 StartY=8 StartZ=0 EndX=134.295 EndY=8 EndZ=0
    g3: LineSegment StartX=-15.7047 StartY=-8 StartZ=0 EndX=134.295 EndY=-8 EndZ=0
    g4: GeomPoint X=59.2953 Y=4e-16 Z=0
    g5: GeomPoint X=148.591 Y=-2 Z=0
    g6: LineSegment [constr] StartX=59.2953 StartY=8 StartZ=0 EndX=59.2953 EndY=-8 EndZ=0
  constraints (15):
    c: Tangent(g0,g2) = 1.5708
    c: Tangent(g0,g3) = -1.5708
    c: Tangent(g1,g2) = 1.5708
    c: Tangent(g1,g3) = -1.5708
    c: Equal(g0,g1)
    c: Horizontal(g3)
    c: Radius(g0) = 8
    c: PointOnObject(g0,g-1)
    c: DistanceX(g0,g1) = 150
    c: PointOnObject(g5,g-4)
    c: Symmetric(g5,g-3,g4)
    c: Horizontal(g1,g4)
    c: Symmetric(g2,g2,g6)
    c: Symmetric(g3,g3,g6)
    c: PointOnObject(g4,g6)
FEATURE [PartDesign::Pocket] Pocket105
  BaseFeature = -> Fillet002
  Direction = (0,0,-1)
  Length = 12
  Length2 = 5
  Placement = pos=(0,0,0) rot=(1,1,1;2.0944rad)
  Profile = -> Sketch258
  ReferenceAxis = -> Sketch258 [N_Axis]
  Suppressed = false
  Type = 0
FEATURE [PartDesign::Body] Body089  label="anti_colision_telemetre"
  AllowCompound = false
  Group = -> [Sketch257,Pad127,Fillet002,Sketch258,Pocket105]
  Origin = -> Origin292
  Placement = pos=(173,-150,39) rot=(0,0,1;4.71239rad)
  Tip = -> Pocket105
FEATURE [App::Link] Link007  label="anti_colision_telemetre001"
  LinkPlacement = pos=(0,300,0) rot=(0,0,1;0rad)
  LinkTransform = true
  LinkedObject = -> Body089
  Placement = pos=(0,300,0) rot=(0,0,1;0rad)
FEATURE [App::Part] Part002005  label="partie_fixe"
  Group = -> [Part002003,InvoluteRack,Body073,Body083,Link002,Body078,Body088,Body080,Link001,Body081,Part002008,Part002009,Body089,Link007]
  Origin = -> Origin270
FEATURE [App::Part] Part002004  label="elevateur_canettes"
  Group = -> [Part002005,Part002006,VarSet]
  Origin = -> Origin267
  Placement = pos=(0,0,0) rot=(0.57735,-0.57735,0.57735;2.0944rad)

RESOLVED EXTERNAL PARTS (link-assembly join: the EXTERNAL_REF files above that resolve inside this repo's crawl, each included once):
---- part CanaPince.FCStd = doc fcstd_e8dda8978ace (77004 chars; too large to inline — full recipe in that document) ----
